FCSTD DOCUMENT  (FreeCAD 0.19R23578 (Git))
Label: enclosure_assembly
License: All rights reserved
LicenseURL: http://en.wikipedia.org/wiki/All_rights_reserved
objects: App::Link×8, App::DocumentObjectGroup×2, PartDesign::CoordinateSystem×1, App::FeaturePython×1, App::Part×1
note: 1 computed .brp shape members not serialized (recipe doc carries the construction recipe); baked Part::Feature solids carry a one-line shape summary decoded from their .brp
EXTERNAL_REF file=enclosure_sheetmetal.FCStd obj=LCS_4
EXTERNAL_REF file=enclosure_sheetmetal.FCStd obj=Body
EXTERNAL_REF file=enclosure_sheetmetal.FCStd obj=LCS_5
EXTERNAL_REF file=enclosure_windows.FCStd obj=LCS_1
EXTERNAL_REF file=enclosure_windows.FCStd obj=Body001
EXTERNAL_REF file=enclosure_hinges.FCStd obj=LCS_1
EXTERNAL_REF file=enclosure_sheetmetal.FCStd obj=LCS_7
EXTERNAL_REF file=enclosure_hinges.FCStd obj=Body001
EXTERNAL_REF file=enclosure_sheetmetal.FCStd obj=LCS_6
EXTERNAL_REF file=enclosure_hinges.FCStd obj=LCS_4
EXTERNAL_REF file=enclosure_hinges.FCStd obj=LCS_7
EXTERNAL_REF file=enclosure_hinges.FCStd obj=Body002
EXTERNAL_REF file=enclosure_hinges.FCStd obj=LCS_6
EXTERNAL_REF file=enclosure_sheetmetal.FCStd obj=LCS_3
EXTERNAL_REF file=enclosure_sheetmetal.FCStd obj=LCS_2
EXTERNAL_REF file=enclosure_sheetmetal.FCStd obj=Body001
EXTERNAL_REF file=enclosure_sheetmetal.FCStd obj=LCS_1
EXTERNAL_REF file=enclosure_windows.FCStd obj=LCS_2
EXTERNAL_REF file=enclosure_windows.FCStd obj=Body

FEATURE [App::DocumentObjectGroup] Parts
FEATURE [PartDesign::CoordinateSystem] LCS_Origin
  AttacherType = Attacher::AttachEngine3D
  MapMode = 2
  Support = -> [X_Axis]
FEATURE [App::DocumentObjectGroup] Constraints
FEATURE [App::FeaturePython] Variables  # WARN: FeaturePython — macro-defined, semantics opaque (R4)
FEATURE [App::Link] enclosure_sheetmetal_main_housing
  AssemblyType = Asm4EE
  AttachedBy = #LCS_4
  AttachedTo = Parent Assembly#LCS_Origin
  AttachmentOffset = pos=(0,0,0) rot=(0.707107,0,0.707107;3.14159rad)
  LinkPlacement = pos=(0,304.8,-3.73e-14) rot=(0.707107,0,0.707107;3.14159rad)
  LinkedObject = -> <external enclosure_sheetmetal.FCStd>#Body
  Placement = pos=(0,304.8,-3.73e-14) rot=(0.707107,0,0.707107;3.14159rad)
  expr: Placement = LCS_Origin.Placement * AttachmentOffset * enclosure_sheetmetal#LCS_4.Placement ^ -1
FEATURE [App::Link] enclosure_windows_top_acrylic_panel
  AssemblyType = Asm4EE
  AttachedBy = #LCS_1
  AttachedTo = enclosure_sheetmetal_main_housing#LCS_5
  AttachmentOffset = pos=(0,0,0) rot=(0,0,1;1.5708rad)
  LinkPlacement = pos=(298,2.6933e-12,573.5) rot=(0,0,-1;4.71239rad)
  LinkedObject = -> <external enclosure_windows.FCStd>#Body001
  Placement = pos=(298,2.6933e-12,573.5) rot=(0,0,-1;4.71239rad)
  expr: Placement = enclosure_sheetmetal_main_housing.Placement * enclosure_sheetmetal#LCS_5.Placement * AttachmentOffset * enclosure_windows#LCS_1.Placement ^ -1
FEATURE [App::Link] enclosure_hinges_Hinge_A
  AssemblyType = Asm4EE
  AttachedBy = #LCS_1
  AttachedTo = enclosure_sheetmetal_main_housing#LCS_7
  LinkPlacement = pos=(107.95,-306.8,514.35) rot=(-1,0,0;4.71239rad)
  LinkedObject = -> <external enclosure_hinges.FCStd>#Body001
  Placement = pos=(107.95,-306.8,514.35) rot=(-1,0,0;4.71239rad)
  expr: Placement = enclosure_sheetmetal_main_housing.Placement * enclosure_sheetmetal#LCS_7.Placement * AttachmentOffset * enclosure_hinges#LCS_1.Placement ^ -1
FEATURE [App::Link] enclosure_hinges_Hinge_A001
  AssemblyType = Asm4EE
  AttachedBy = #LCS_1
  AttachedTo = enclosure_sheetmetal_main_housing#LCS_6
  LinkPlacement = pos=(107.95,-306.8,95.25) rot=(-1,0,0;4.71239rad)
  LinkedObject = -> <external enclosure_hinges.FCStd>#Body001
  Placement = pos=(107.95,-306.8,95.25) rot=(-1,0,0;4.71239rad)
  expr: Placement = enclosure_sheetmetal_main_housing.Placement * enclosure_sheetmetal#LCS_6.Placement * AttachmentOffset * enclosure_hinges#LCS_1.Placement ^ -1
FEATURE [App::Link] enclosure_hinges_Hinge_B
  AssemblyType = Asm4EE
  AttachedBy = #LCS_7
  AttachedTo = enclosure_hinges_Hinge_A#LCS_4
  LinkPlacement = pos=(127,-325.85,476.25) rot=(0.57735,0.57735,-0.57735;4.18879rad)
  LinkedObject = -> <external enclosure_hinges.FCStd>#Body002
  Placement = pos=(127,-325.85,476.25) rot=(0.57735,0.57735,-0.57735;4.18879rad)
  expr: Placement = enclosure_hinges_Hinge_A.Placement * enclosure_hinges#LCS_4.Placement * AttachmentOffset * enclosure_hinges#LCS_7.Placement ^ -1
FEATURE [App::Link] enclosure_hinges_Hinge_B001
  AssemblyType = Asm4EE
  AttachedBy = #LCS_6
  AttachedTo = enclosure_sheetmetal_door#LCS_3
  AttachmentOffset = pos=(0,0,0) rot=(1,0,0;3.14159rad)
  LinkPlacement = pos=(127,-325.85,57.15) rot=(-0.57735,-0.57735,0.57735;2.0944rad)
  LinkedObject = -> <external enclosure_hinges.FCStd>#Body002
  Placement = pos=(127,-325.85,57.15) rot=(-0.57735,-0.57735,0.57735;2.0944rad)
  expr: Placement = enclosure_sheetmetal_door.Placement * enclosure_sheetmetal#LCS_3.Placement * AttachmentOffset * enclosure_hinges#LCS_6.Placement ^ -1
FEATURE [App::Link] enclosure_sheetmetal_door
  AssemblyType = Asm4EE
  AttachedBy = #LCS_2
  AttachedTo = enclosure_hinges_Hinge_B#LCS_6
  AttachmentOffset = pos=(0,0,0) rot=(1,0,0;3.14159rad)
  LinkPlacement = pos=(129,-346.9,571.5) rot=(1,0,0;4.71239rad)
  LinkedObject = -> <external enclosure_sheetmetal.FCStd>#Body001
  Placement = pos=(129,-346.9,571.5) rot=(1,0,0;4.71239rad)
  expr: Placement = enclosure_hinges_Hinge_B.Placement * enclosure_hinges#LCS_6.Placement * AttachmentOffset * enclosure_sheetmetal#LCS_2.Placement ^ -1
FEATURE [App::Link] enclosure_windows_side_acrylic_panel
  AssemblyType = Asm4EE
  AttachedBy = #LCS_2
  AttachedTo = enclosure_sheetmetal_door#LCS_1
  AttachmentOffset = pos=(0,0,0) rot=(0,0,1;3.14159rad)
  LinkPlacement = pos=(757.6,-346.9,284.75) rot=(0,-0.707107,-0.707107;3.14159rad)
  LinkedObject = -> <external enclosure_windows.FCStd>#Body
  Placement = pos=(757.6,-346.9,284.75) rot=(0,-0.707107,-0.707107;3.14159rad)
  expr: Placement = enclosure_sheetmetal_door.Placement * enclosure_sheetmetal#LCS_1.Placement * AttachmentOffset * enclosure_windows#LCS_2.Placement ^ -1
FEATURE [App::Part] Model
  Configuration = 0
  Group = -> [LCS_Origin,Constraints,Variables,enclosure_sheetmetal_main_housing,enclosure_windows_top_acrylic_panel,enclosure_hinges_Hinge_A,enclosure_hinges_Hinge_A001,enclosure_hinges_Hinge_B,enclosure_hinges_Hinge_B001,enclosure_sheetmetal_door,enclosure_windows_side_acrylic_panel]
  Origin = -> Origin
  Type = Assembly4 Model

RESOLVED EXTERNAL PARTS (link-assembly join: the EXTERNAL_REF files above that resolve inside this repo's crawl, each included once):
---- part enclosure_hinges.FCStd = doc fcstd_d395666c116b ----
FCSTD DOCUMENT  (FreeCAD 0.19R23578 (Git))
Label: enclosure_hinges
License: All rights reserved
LicenseURL: http://en.wikipedia.org/wiki/All_rights_reserved
objects: PartDesign::CoordinateSystem×11, Sketcher::SketchObject×10, PartDesign::Fillet×5, PartDesign::Pocket×4, PartDesign::Pad×3, PartDesign::Body×3, PartDesign::Hole×2, PartDesign::Revolution×1
note: 54 computed .brp shape members not serialized (recipe doc carries the construction recipe); baked Part::Feature solids carry a one-line shape summary decoded from their .brp

FEATURE [Sketcher::SketchObject] Sketch004
  MapMode = 5
  Placement = pos=(0,0,0) rot=(1,0,0;1.5708rad)
  Support = -> [XZ_Plane003]
  expr: Constraints[7] = 0.375"
  expr: Constraints[8] = 0.375"
  sketch-geometry (7):
    g0: LineSegment StartX=-8.37762 StartY=2.44 StartZ=0 EndX=6.54086 EndY=13.5368 EndZ=0
    g1: ArcOfCircle CenterX=9.525 CenterY=9.525 CenterZ=0 NormalX=0 NormalY=0 NormalZ=1 AngleXU=0 Radius=5 StartAngle=5.35193 EndAngle=8.49352
    g2: LineSegment StartX=12.5091 StartY=5.51315 StartZ=0 EndX=8.37762 EndY=2.44 EndZ=0
    g3: LineSegment StartX=8.37762 StartY=2.44 StartZ=0 EndX=8.37762 EndY=0 EndZ=0
    g4: Circle CenterX=9.525 CenterY=9.525 CenterZ=0 NormalX=0 NormalY=0 NormalZ=1 AngleXU=0 Radius=2.55
    g5: LineSegment StartX=-8.37762 StartY=2.44 StartZ=0 EndX=-8.37762 EndY=0 EndZ=0
    g6: LineSegment StartX=8.37762 StartY=0 StartZ=0 EndX=-8.37762 EndY=0 EndZ=0
  constraints (18):
    c: Coincident(g3,g2)
    c: Vertical(g3)
    c: Tangent(g2,g1) = 1.5708
    c: Tangent(g1,g0) = 1.5708
    c: Diameter(g1) = 10
    c: Coincident(g4,g1)
    c: Diameter(g4) = 5.1
    c: DistanceX(g-1,g1) = 9.525
    c: DistanceY(g-1,g1) = 9.525
    c: Parallel(g0,g2)
    c: Coincident(g5,g0)
    c: PointOnObject(g5,g-1)
    c: Coincident(g6,g3)
    c: Coincident(g6,g5)
    c: Vertical(g5)
    c: Equal(g5,g3)
    c: DistanceY(g3,g3) = 2.44
    c: Symmetric(g5,g3,g-2)
FEATURE [PartDesign::Pad] Pad001
  Direction = (1,1,1)
  Length = 38.1
  Length2 = 100
  Placement = pos=(0,0,0) rot=(1,0,0;1.5708rad)
  Profile = -> Sketch004
  Type = 0
  expr: Length = 1.5"
FEATURE [Sketcher::SketchObject] Sketch005
  AttachmentOffset = pos=(0,0,22.44) rot=(0,0,1;0rad)
  MapMode = 5
  Placement = pos=(0,0,22.44) rot=(0,0,1;0rad)
  Support = -> [XY_Plane003]
  expr: Constraints[8] = Pad001.Length / 2
  expr: Constraints[10] = 5.25mm
  sketch-geometry (4):
    g0: Circle CenterX=0 CenterY=-6.35 CenterZ=0 NormalX=0 NormalY=0 NormalZ=1 AngleXU=0 Radius=2.625
    g1: Circle CenterX=0 CenterY=-31.75 CenterZ=0 NormalX=0 NormalY=0 NormalZ=1 AngleXU=0 Radius=2.625
    g2: LineSegment StartX=0 StartY=-6.35 StartZ=0 EndX=0 EndY=-19.05 EndZ=0
    g3: LineSegment StartX=0 StartY=-19.05 StartZ=0 EndX=0 EndY=-31.75 EndZ=0
  constraints (11):
    c: PointOnObject(g0,g-2)
    c: PointOnObject(g1,g-2)
    c: DistanceY(g1,g0) = 25.4
    c: Coincident(g2,g0)
    c: PointOnObject(g2,g-2)
    c: Coincident(g3,g2)
    c: Coincident(g3,g1)
    c: Equal(g2,g3)
    c: DistanceY(g2,g-1) = 19.05
    c: Equal(g0,g1)
    c: Diameter(g0) = 5.25
FEATURE [PartDesign::Hole] Hole001
  BaseFeature = -> Pad001
  Depth = 25
  DepthType = 1
  Diameter = 6
  DrillPoint = 1
  DrillPointAngle = 118
  HoleCutCountersinkAngle = 90
  HoleCutDepth = 20
  HoleCutDiameter = 11
  HoleCutType = 1
  ModelActualThread = false
  Placement = pos=(0,0,0) rot=(1,0,0;1.5708rad)
  Profile = -> Sketch005
  Tapered = false
  TaperedAngle = 90
  ThreadAngle = 0
  ThreadClass = 0
  ThreadCutOffInner = 0
  ThreadCutOffOuter = 0
  ThreadDirection = 0
  ThreadFit = 0
  ThreadPitch = 0
  ThreadSize = 0
  ThreadType = 0
  Threaded = false
FEATURE [Sketcher::SketchObject] Sketch006
  MapMode = 5
  Placement = pos=(0,0,0) rot=(0.57735,0.57735,0.57735;2.0944rad)
  Support = -> [YZ_Plane003]
  expr: Constraints[11] = Pad001.Length / 2
  expr: Constraints[8] = Pad001.Length / 3
  sketch-geometry (5):
    g0: LineSegment StartX=-12.7 StartY=2.44 StartZ=0 EndX=-25.4 EndY=2.44 EndZ=0
    g1: LineSegment StartX=-25.4 StartY=2.44 StartZ=0 EndX=-25.4 EndY=22.44 EndZ=0
    g2: LineSegment StartX=-25.4 StartY=22.44 StartZ=0 EndX=-12.7 EndY=22.44 EndZ=0
    g3: LineSegment StartX=-12.7 StartY=22.44 StartZ=0 EndX=-12.7 EndY=2.44 EndZ=0
    g4: LineSegment StartX=-19.05 StartY=22.44 StartZ=0 EndX=-19.05 EndY=2.44 EndZ=0
  constraints (15):
    c: Coincident(g0,g1)
    c: Coincident(g1,g2)
    c: Coincident(g2,g3)
    c: Coincident(g3,g0)
    c: Horizontal(g0)
    c: Horizontal(g2)
    c: Vertical(g1)
    c: Vertical(g3)
    c: DistanceX(g2,g2) = 12.7
    c: PointOnObject(g4,g2)
    c: PointOnObject(g4,g0)
    c: DistanceX(g4,g-1) = 19.05
    c: Symmetric(g2,g1,g4)
    c: DistanceY(g3,g3) = 20
    c: DistanceY(g-1,g0) = 2.44
FEATURE [PartDesign::Pocket] Pocket001
  BaseFeature = -> Hole001
  Length = 5
  Length2 = 100
  Midplane = true
  Placement = pos=(0,0,0) rot=(1,0,0;1.5708rad)
  Profile = -> Sketch006
  Type = 1
FEATURE [Sketcher::SketchObject] Sketch007
  AttachmentOffset = pos=(0,0,22.44) rot=(0,0,1;0rad)
  MapMode = 5
  Placement = pos=(0,0,22.44) rot=(0,0,1;0rad)
  Support = -> [XY_Plane004]
  expr: Constraints[10] = 5.25mm
  expr: Constraints[8] = Pad002.Length / 2
  sketch-geometry (4):
    g0: Circle CenterX=0 CenterY=-6.35 CenterZ=0 NormalX=0 NormalY=0 NormalZ=1 AngleXU=0 Radius=2.625
    g1: Circle CenterX=0 CenterY=-31.75 CenterZ=0 NormalX=0 NormalY=0 NormalZ=1 AngleXU=0 Radius=2.625
    g2: LineSegment StartX=0 StartY=-6.35 StartZ=0 EndX=0 EndY=-19.05 EndZ=0
    g3: LineSegment StartX=0 StartY=-19.05 StartZ=0 EndX=0 EndY=-31.75 EndZ=0
  constraints (11):
    c: PointOnObject(g0,g-2)
    c: PointOnObject(g1,g-2)
    c: DistanceY(g1,g0) = 25.4
    c: Coincident(g2,g0)
    c: PointOnObject(g2,g-2)
    c: Coincident(g3,g2)
    c: Coincident(g3,g1)
    c: Equal(g2,g3)
    c: DistanceY(g2,g-1) = 19.05
    c: Equal(g0,g1)
    c: Diameter(g0) = 5.25
FEATURE [Sketcher::SketchObject] Sketch008
  MapMode = 5
  Placement = pos=(0,0,0) rot=(0.57735,0.57735,0.57735;2.0944rad)
  Support = -> [YZ_Plane004]
  expr: Constraints[26] = Pad002.Length / 3 - 0.24mm
  expr: Constraints[24] = Pad002.Length / 2
  sketch-geometry (9):
    g0: LineSegment StartX=-25.28 StartY=2.44 StartZ=0 EndX=-45.28 EndY=2.44 EndZ=0
    g1: LineSegment StartX=-45.28 StartY=2.44 StartZ=0 EndX=-45.28 EndY=22.44 EndZ=0
    g2: LineSegment StartX=-45.28 StartY=22.44 StartZ=0 EndX=-25.28 EndY=22.44 EndZ=0
    g3: LineSegment StartX=-25.28 StartY=22.44 StartZ=0 EndX=-25.28 EndY=2.44 EndZ=0
    g4: LineSegment StartX=-12.82 StartY=2.44 StartZ=0 EndX=7.18 EndY=2.44 EndZ=0
    g5: LineSegment StartX=7.18 StartY=2.44 StartZ=0 EndX=7.18 EndY=22.44 EndZ=0
    g6: LineSegment StartX=7.18 StartY=22.44 StartZ=0 EndX=-12.82 EndY=22.44 EndZ=0
    g7: LineSegment StartX=-12.82 StartY=22.44 StartZ=0 EndX=-12.82 EndY=2.44 EndZ=0
    g8: LineSegment StartX=-19.05 StartY=22.44 StartZ=0 EndX=-19.05 EndY=2.44 EndZ=0
  constraints (27):
    c: Coincident(g0,g1)
    c: Coincident(g1,g2)
    c: Coincident(g2,g3)
    c: Coincident(g3,g0)
    c: Horizontal(g0)
    c: Horizontal(g2)
    c: Vertical(g1)
    c: Vertical(g3)
    c: Coincident(g4,g5)
    c: Coincident(g5,g6)
    c: Coincident(g6,g7)
    c: Coincident(g7,g4)
    c: Horizontal(g4)
    c: Horizontal(g6)
    c: Vertical(g5)
    c: Vertical(g7)
    c: Horizontal(g6,g2)
    c: Horizontal(g0,g4)
    c: Equal(g4,g0)
    c: DistanceY(g1,g1) = 20
    c: DistanceX(g2,g2) = 20
    c: Horizontal(g8,g2)
    c: Horizontal(g0,g8)
    c: Symmetric(g6,g2,g8)
    c: DistanceX(g8,g-1) = 19.05
    c: DistanceY(g-1,g4) = 2.44
    c: DistanceX(g2,g6) = 12.46
FEATURE [Sketcher::SketchObject] Sketch009
  MapMode = 5
  Placement = pos=(0,0,0) rot=(1,0,0;1.5708rad)
  Support = -> [XZ_Plane005]
  expr: Constraints[8] = 0.375"
  expr: Constraints[7] = 0.375"
  sketch-geometry (7):
    g0: LineSegment StartX=-8.37762 StartY=2.44 StartZ=0 EndX=6.54086 EndY=13.5368 EndZ=0
    g1: ArcOfCircle CenterX=9.525 CenterY=9.525 CenterZ=0 NormalX=0 NormalY=0 NormalZ=1 AngleXU=0 Radius=5 StartAngle=5.35193 EndAngle=8.49352
    g2: LineSegment StartX=12.5091 StartY=5.51315 StartZ=0 EndX=8.37762 EndY=2.44 EndZ=0
    g3: LineSegment StartX=8.37762 StartY=2.44 StartZ=0 EndX=8.37762 EndY=0 EndZ=0
    g4: Circle CenterX=9.525 CenterY=9.525 CenterZ=0 NormalX=0 NormalY=0 NormalZ=1 AngleXU=0 Radius=2.55
    g5: LineSegment StartX=-8.37762 StartY=2.44 StartZ=0 EndX=-8.37762 EndY=0 EndZ=0
    g6: LineSegment StartX=8.37762 StartY=0 StartZ=0 EndX=-8.37762 EndY=0 EndZ=0
  constraints (18):
    c: Coincident(g3,g2)
    c: Vertical(g3)
    c: Tangent(g2,g1) = 1.5708
    c: Tangent(g1,g0) = 1.5708
    c: Diameter(g1) = 10
    c: Coincident(g4,g1)
    c: Diameter(g4) = 5.1
    c: DistanceX(g-1,g1) = 9.525
    c: DistanceY(g-1,g1) = 9.525
    c: Parallel(g0,g2)
    c: Coincident(g5,g0)
    c: PointOnObject(g5,g-1)
    c: Coincident(g6,g3)
    c: Coincident(g6,g5)
    c: Vertical(g5)
    c: Equal(g5,g3)
    c: DistanceY(g3,g3) = 2.44
    c: Symmetric(g5,g3,g-2)
FEATURE [PartDesign::Pad] Pad002
  Direction = (1,1,1)
  Length = 38.1
  Length2 = 100
  Placement = pos=(0,0,0) rot=(1,0,0;1.5708rad)
  Profile = -> Sketch009
  Type = 0
  expr: Length = 1.5"
FEATURE [PartDesign::Hole] Hole002
  BaseFeature = -> Pad002
  Depth = 25
  DepthType = 1
  Diameter = 6
  DrillPoint = 1
  DrillPointAngle = 118
  HoleCutCountersinkAngle = 90
  HoleCutDepth = 20
  HoleCutDiameter = 11
  HoleCutType = 1
  ModelActualThread = false
  Placement = pos=(0,0,0) rot=(1,0,0;1.5708rad)
  Profile = -> Sketch007
  Tapered = false
  TaperedAngle = 90
  ThreadAngle = 0
  ThreadClass = 0
  ThreadCutOffInner = 0
  ThreadCutOffOuter = 0
  ThreadDirection = 0
  ThreadFit = 0
  ThreadPitch = 0
  ThreadSize = 0
  ThreadType = 0
  Threaded = false
FEATURE [PartDesign::Pocket] Pocket002
  BaseFeature = -> Hole002
  Length = 5
  Length2 = 100
  Midplane = true
  Placement = pos=(0,0,0) rot=(1,0,0;1.5708rad)
  Profile = -> Sketch008
  Type = 1
FEATURE [PartDesign::Fillet] Fillet
  Base = -> Pocket002 [Edge33,Edge18,Edge17,Edge32]
  BaseFeature = -> Pocket002
  Placement = pos=(0,0,0) rot=(1,0,0;1.5708rad)
  Radius = 1
  SupportTransform = true
FEATURE [PartDesign::Fillet] Fillet001
  Base = -> Pocket001 [Edge20,Edge10]
  BaseFeature = -> Pocket001
  Placement = pos=(0,0,0) rot=(1,0,0;1.5708rad)
  Radius = 1
  SupportTransform = true
FEATURE [PartDesign::Fillet] Fillet002
  Base = -> Fillet001 [Edge36,Edge21]
  BaseFeature = -> Fillet001
  Placement = pos=(0,0,0) rot=(1,0,0;1.5708rad)
  Radius = 1
  SupportTransform = true
FEATURE [PartDesign::Fillet] Fillet003
  Base = -> Fillet [Edge9,Edge28]
  BaseFeature = -> Fillet
  Placement = pos=(0,0,0) rot=(1,0,0;1.5708rad)
  Radius = 1
  SupportTransform = true
FEATURE [Sketcher::SketchObject] Sketch
  MapMode = 5
  Support = -> [XY_Plane006]
  expr: Constraints[11] = 1.5in
  sketch-geometry (7):
    g0: LineSegment StartX=2.55 StartY=19.05 StartZ=0 EndX=5 EndY=19.05 EndZ=0
    g1: LineSegment StartX=5 StartY=19.05 StartZ=0 EndX=19.6187 EndY=4.43129 EndZ=0
    g2: LineSegment StartX=19.6187 StartY=4.43129 StartZ=0 EndX=19.6187 EndY=-4.43129 EndZ=0
    g3: LineSegment StartX=19.6187 StartY=-4.43129 StartZ=0 EndX=5 EndY=-19.05 EndZ=0
    g4: LineSegment StartX=5 StartY=-19.05 StartZ=0 EndX=2.55 EndY=-19.05 EndZ=0
    g5: LineSegment StartX=2.55 StartY=-19.05 StartZ=0 EndX=2.55 EndY=19.05 EndZ=0
    g6: LineSegment StartX=-9.05314 StartY=0 StartZ=0 EndX=28.1994 EndY=0 EndZ=0
  constraints (16):
    c: Horizontal(g0)
    c: Coincident(g0,g1)
    c: Coincident(g1,g2)
    c: Coincident(g2,g3)
    c: Coincident(g3,g4)
    c: Coincident(g4,g5)
    c: Coincident(g5,g0)
    c: Horizontal(g6)
    c: Symmetric(g0,g4,g6)
    c: Symmetric(g3,g0,g6)
    c: Symmetric(g1,g2,g6)
    c: DistanceY(g5,g5) = 38.1
    c: DistanceX(g-1,g0) = 2.55
    c: Angle(g5,g1) = 0.785398
    c: DistanceX(g-1,g0) = 5
    c: PointOnObject(g6,g-1)
FEATURE [PartDesign::Revolution] Revolution
  Angle = 360
  Axis = (0,1,0)
  Base = (0,0,0)
  Profile = -> Sketch
  ReferenceAxis = -> Sketch [V_Axis]
  Reversed = true
FEATURE [Sketcher::SketchObject] Sketch010
  MapMode = 5
  Placement = pos=(0,0,0) rot=(1,0,0;1.5708rad)
  Support = -> [XZ_Plane006]
  sketch-geometry (8):
    g0: ArcOfCircle CenterX=0 CenterY=0 CenterZ=0 NormalX=0 NormalY=0 NormalZ=1 AngleXU=0 Radius=5 StartAngle=1.5708 EndAngle=4.71239
    g1: LineSegment StartX=3e-16 StartY=5 StartZ=0 EndX=76.4224 EndY=5 EndZ=0
    g2: LineSegment StartX=76.4224 StartY=5 StartZ=0 EndX=76.4224 EndY=50.1076 EndZ=0
    g3: LineSegment StartX=76.4224 StartY=50.1076 StartZ=0 EndX=-42.6385 EndY=50.1076 EndZ=0
    g4: LineSegment StartX=-42.6385 StartY=50.1076 StartZ=0 EndX=-42.6385 EndY=-50.303 EndZ=0
    g5: LineSegment StartX=-42.6385 StartY=-50.303 StartZ=0 EndX=76.4224 EndY=-50.303 EndZ=0
    g6: LineSegment StartX=76.4224 StartY=-50.303 StartZ=0 EndX=76.4224 EndY=-5 EndZ=0
    g7: LineSegment StartX=76.4224 StartY=-5 StartZ=0 EndX=0 EndY=-5 EndZ=0
  constraints (20):
    c: Coincident(g0,g-1)
    c: PointOnObject(g0,g-2)
    c: PointOnObject(g0,g-2)
    c: Coincident(g1,g0)
    c: Horizontal(g1)
    c: Coincident(g1,g2)
    c: Vertical(g2)
    c: Coincident(g2,g3)
    c: Horizontal(g3)
    c: Coincident(g3,g4)
    c: Vertical(g4)
    c: Coincident(g4,g5)
    c: Horizontal(g5)
    c: Coincident(g5,g6)
    c: Coincident(g6,g7)
    c: Coincident(g7,g0)
    c: Horizontal(g7)
    c: Vertical(g6)
    c: Vertical(g6,g1)
    c: Radius(g0) = 5
FEATURE [PartDesign::Pocket] Pocket
  BaseFeature = -> Revolution
  Length = 5
  Length2 = 100
  Midplane = true
  Profile = -> Sketch010
  Type = 1
FEATURE [Sketcher::SketchObject] Sketch011
  MapMode = 5
  Placement = pos=(0,0,0) rot=(1,0,0;1.5708rad)
  Support = -> [XZ_Plane006]
  expr: Constraints[11] = 1in
  sketch-geometry (5):
    g0: Circle CenterX=25.4 CenterY=0 CenterZ=0 NormalX=0 NormalY=0 NormalZ=1 AngleXU=0 Radius=2.55
    g1: ArcOfCircle CenterX=25.4 CenterY=0 CenterZ=0 NormalX=0 NormalY=0 NormalZ=1 AngleXU=0 Radius=5 StartAngle=4.71239 EndAngle=7.85398
    g2: LineSegment StartX=25.4 StartY=5 StartZ=0 EndX=7 EndY=5 EndZ=0
    g3: LineSegment StartX=7 StartY=5 StartZ=0 EndX=7 EndY=-5 EndZ=0
    g4: LineSegment StartX=7 StartY=-5 StartZ=0 EndX=25.4 EndY=-5 EndZ=0
  constraints (13):
    c: PointOnObject(g0,g-1)
    c: Coincident(g1,g0)
    c: Tangent(g1,g2) = -1.5708
    c: Coincident(g2,g3)
    c: Coincident(g3,g4)
    c: Tangent(g4,g1) = -1.5708
    c: Horizontal(g2)
    c: Horizontal(g4)
    c: Vertical(g3)
    c: Diameter(g0) = 5.1
    c: Diameter(g1) = 10
    c: DistanceX(g-1,g0) = 25.4
    c: DistanceX(g-1,g2) = 7
FEATURE [PartDesign::Pad] Pad
  BaseFeature = -> Pocket
  Direction = (1,1,1)
  Length = 12.46
  Length2 = 100
  Midplane = true
  Profile = -> Sketch011
  Type = 0
  expr: Length = Pad002.Length / 3 - 0.24mm
FEATURE [Sketcher::SketchObject] Sketch012
  MapMode = 5
  Support = -> [XY_Plane006]
  expr: Constraints[12] = Pad001.Length / 3
  sketch-geometry (6):
    g0: LineSegment StartX=-20.0307 StartY=6.35 StartZ=0 EndX=5 EndY=6.35 EndZ=0
    g1: LineSegment StartX=6 StartY=5.35 StartZ=0 EndX=6 EndY=-5.35 EndZ=0
    g2: LineSegment StartX=5 StartY=-6.35 StartZ=0 EndX=-20.0307 EndY=-6.35 EndZ=0
    g3: LineSegment StartX=-20.0307 StartY=-6.35 StartZ=0 EndX=-20.0307 EndY=6.35 EndZ=0
    g4: ArcOfCircle CenterX=5 CenterY=5.35 CenterZ=0 NormalX=0 NormalY=0 NormalZ=1 AngleXU=0 Radius=1 StartAngle=0 EndAngle=1.5708
    g5: ArcOfCircle CenterX=5 CenterY=-5.35 CenterZ=0 NormalX=0 NormalY=0 NormalZ=1 AngleXU=0 Radius=1 StartAngle=4.71239 EndAngle=6.28319
  constraints (14):
    c: Coincident(g2,g3)
    c: Coincident(g3,g0)
    c: Horizontal(g0)
    c: Horizontal(g2)
    c: Vertical(g1)
    c: Symmetric(g0,g2,g-1)
    c: Tangent(g0,g4) = 1.5708
    c: Tangent(g1,g4) = 1.5708
    c: Tangent(g1,g5) = 1.5708
    c: Tangent(g2,g5) = 1.5708
    c: Radius(g5) = 1
    c: Equal(g4,g5)
    c: DistanceY(g3,g3) = 12.7
    c: DistanceX(g-1,g1) = 6
FEATURE [PartDesign::Pocket] Pocket003
  BaseFeature = -> Pad
  Length = 5
  Length2 = 100
  Midplane = true
  Profile = -> Sketch012
  Type = 1
FEATURE [PartDesign::Fillet] Fillet004
  Base = -> Pocket003 [Edge14,Edge8,Edge55,Edge63]
  BaseFeature = -> Pocket003
  Radius = 2
  SupportTransform = false
FEATURE [PartDesign::CoordinateSystem] LCS_1
  AttacherType = Attacher::AttachEngine3D
  MapMode = 45
  Placement = pos=(2e-16,-19.05,0) rot=(0,0,1;0rad)
  Support = -> [Pad001]
FEATURE [PartDesign::CoordinateSystem] LCS_2
  AttacherType = Attacher::AttachEngine3D
  MapMode = 11
  Placement = pos=(0,-6.35,2.44) rot=(0,0,1;1.5708rad)
  Support = -> [Hole001]
FEATURE [PartDesign::CoordinateSystem] LCS_3
  AttacherType = Attacher::AttachEngine3D
  MapMode = 11
  Placement = pos=(0,-31.75,2.44) rot=(0,0,1;1.5708rad)
  Support = -> [Hole001]
FEATURE [PartDesign::CoordinateSystem] LCS_4
  AttacherType = Attacher::AttachEngine3D
  MapMode = 45
  Placement = pos=(9.525,-19.05,9.525) rot=(0,0.707107,0.707107;3.14159rad)
  Support = -> [Pad001]
FEATURE [PartDesign::CoordinateSystem] LCS_5
  AttacherType = Attacher::AttachEngine3D
  AttachmentOffset = pos=(0,0,19.05) rot=(0,0,1;0rad)
  MapMode = 11
  Placement = pos=(9.525,-19.05,9.525) rot=(0.57735,-0.57735,0.57735;2.0944rad)
  Support = -> [Sketch004]
  expr: .AttachmentOffset.Base.z = 0.5 * Pad001.Length
FEATURE [PartDesign::Body] Body001  label="Hinge_A"
  Group = -> [Sketch004,Pad001,Sketch005,Hole001,Sketch006,Pocket001,Fillet001,Fillet002,LCS_1,LCS_2,LCS_3,LCS_4,LCS_5]
  Origin = -> Origin003
  Tip = -> Fillet002
FEATURE [PartDesign::CoordinateSystem] LCS_6
  AttacherType = Attacher::AttachEngine3D
  MapMode = 45
  Placement = pos=(2e-16,-19.05,0) rot=(0,0,1;0rad)
  Support = -> [Pad002]
FEATURE [PartDesign::CoordinateSystem] LCS_7
  AttacherType = Attacher::AttachEngine3D
  AttachmentOffset = pos=(0,0,19.05) rot=(0,0,1;0rad)
  MapMode = 11
  Placement = pos=(9.525,-19.05,9.525) rot=(0.57735,-0.57735,0.57735;2.0944rad)
  Support = -> [Sketch009]
  expr: .AttachmentOffset.Base.z = Pad002.Length / 2
FEATURE [PartDesign::CoordinateSystem] LCS_8
  AttacherType = Attacher::AttachEngine3D
  MapMode = 11
  Placement = pos=(0,-6.35,2.44) rot=(0,0,1;1.5708rad)
  Support = -> [Hole002]
FEATURE [PartDesign::CoordinateSystem] LCS_9
  AttacherType = Attacher::AttachEngine3D
  MapMode = 11
  Placement = pos=(0,-31.75,2.44) rot=(0,0,1;1.5708rad)
  Support = -> [Hole002]
FEATURE [PartDesign::Body] Body002  label="Hinge_B"
  Group = -> [Sketch009,Pad002,Sketch007,Hole002,Sketch008,Pocket002,Fillet,Fillet003,LCS_6,LCS_7,LCS_8,LCS_9]
  Origin = -> Origin005
  Tip = -> Fillet003
FEATURE [PartDesign::CoordinateSystem] LCS_10
  AttacherType = Attacher::AttachEngine3D
  MapMode = 5
  Support = -> [XY_Plane006]
FEATURE [PartDesign::CoordinateSystem] LCS_11
  AttacherType = Attacher::AttachEngine3D
  MapMode = 11
  Placement = pos=(25.4,0,0) rot=(0.57735,-0.57735,0.57735;2.0944rad)
  Support = -> [Sketch011]
FEATURE [PartDesign::Body] Body  label="Hinge_C"
  Group = -> [Sketch,Revolution,Sketch010,Pocket,Sketch011,Pad,Sketch012,Pocket003,Fillet004,LCS_10,LCS_11]
  Origin = -> Origin006
  Tip = -> Fillet004
---- part enclosure_sheetmetal.FCStd = doc fcstd_4c1e4707e105 ----
FCSTD DOCUMENT  (FreeCAD 0.19R23578 (Git))
Label: enclosure_sheetmetal
License: All rights reserved
LicenseURL: http://en.wikipedia.org/wiki/All_rights_reserved
objects: PartDesign::FeaturePython×10, Sketcher::SketchObject×7, PartDesign::CoordinateSystem×7, PartDesign::Pocket×5, PartDesign::Body×2, PartDesign::Chamfer×1
note: 38 computed .brp shape members not serialized (recipe doc carries the construction recipe); baked Part::Feature solids carry a one-line shape summary decoded from their .brp

FEATURE [Sketcher::SketchObject] Sketch
  MapMode = 5
  Support = -> [XY_Plane001]
  expr: Constraints[9] = 24"
  expr: Constraints[10] = 22.5"
  sketch-geometry (4):
    g0: LineSegment StartX=0 StartY=0 StartZ=0 EndX=571.5 EndY=0 EndZ=0
    g1: LineSegment StartX=571.5 StartY=0 StartZ=0 EndX=571.5 EndY=609.6 EndZ=0
    g2: LineSegment StartX=571.5 StartY=609.6 StartZ=0 EndX=0 EndY=609.6 EndZ=0
    g3: LineSegment StartX=0 StartY=609.6 StartZ=0 EndX=0 EndY=0 EndZ=0
  constraints (11):
    c: Coincident(g0,g1)
    c: Coincident(g1,g2)
    c: Coincident(g2,g3)
    c: Coincident(g3,g0)
    c: Horizontal(g0)
    c: Horizontal(g2)
    c: Vertical(g1)
    c: Vertical(g3)
    c: Coincident(g0,g-1)
    c: DistanceY(g3,g3) = 609.6
    c: DistanceX(g0,g0) = 571.5
FEATURE [PartDesign::FeaturePython] BaseBend  # WARN: FeaturePython — macro-defined, semantics opaque (R4)
  BendSide = 0
  BendSketch = -> Sketch
  length = 100
  radius = 1
  thickness = 1
FEATURE [PartDesign::FeaturePython] Bend  # WARN: FeaturePython — macro-defined, semantics opaque (R4)
  AutoMiter = true
  BaseFeature = -> BaseBend
  BendType = 0
  LengthList = [127]
  ReliefFactor = 0.7
  UseReliefFactor = false
  angle = 90
  baseObject = -> BaseBend [Edge4,Edge10]
  bendAList = [90]
  extend1 = 0
  extend2 = 0
  gap1 = 0
  gap2 = 0
  invert = false
  kfactor = 0.5
  length = 127
  miterangle1 = 0
  miterangle2 = 0
  offset = 0
  radius = 1
  reliefType = 0
  reliefd = 1
  reliefw = 0.8
  sketchflip = false
  sketchinvert = false
  unfold = false
  expr: length = 5"
FEATURE [PartDesign::FeaturePython] Bend001  # WARN: FeaturePython — macro-defined, semantics opaque (R4)
  AutoMiter = true
  BaseFeature = -> Bend
  BendType = 0
  LengthList = [76.2]
  ReliefFactor = 0.7
  UseReliefFactor = false
  angle = 90
  baseObject = -> Bend [Edge43,Edge10]
  bendAList = [90]
  extend1 = 0
  extend2 = 0
  gap1 = 0
  gap2 = 0
  invert = false
  kfactor = 0.5
  length = 76.2
  miterangle1 = 0
  miterangle2 = 0
  offset = 0
  radius = 1
  reliefType = 0
  reliefd = 1
  reliefw = 0.8
  sketchflip = false
  sketchinvert = false
  unfold = false
  expr: length = 3"
FEATURE [PartDesign::FeaturePython] Bend002  # WARN: FeaturePython — macro-defined, semantics opaque (R4)
  AutoMiter = true
  BaseFeature = -> Bend001
  BendType = 0
  LengthList = [457.2]
  ReliefFactor = 0.7
  UseReliefFactor = false
  angle = 90
  baseObject = -> Bend001 [Edge73,Edge9]
  bendAList = [90]
  extend1 = 0
  extend2 = 0
  gap1 = 0
  gap2 = 0
  invert = true
  kfactor = 0.5
  length = 457.2
  miterangle1 = 0
  miterangle2 = 0
  offset = 0
  radius = 1
  reliefType = 0
  reliefd = 1
  reliefw = 0.8
  sketchflip = false
  sketchinvert = false
  unfold = false
  expr: length = 18"
FEATURE [PartDesign::Chamfer] Chamfer
  Angle = 45
  Base = -> Bend002 [Edge100,Edge2,Edge8,Edge108]
  BaseFeature = -> Bend002
  ChamferType = 0
  FlipDirection = false
  Size = 82.55
  Size2 = 1
  SupportTransform = true
  expr: Size = 3.25"
FEATURE [PartDesign::FeaturePython] Bend003  # WARN: FeaturePython — macro-defined, semantics opaque (R4)
  AutoMiter = true
  BaseFeature = -> Chamfer
  BendType = 0
  LengthList = [225.552]
  ReliefFactor = 0.7
  UseReliefFactor = false
  angle = 90
  baseObject = -> Chamfer [Edge11,Edge16,Edge4,Edge18,Edge17,Edge108,Edge117,Edge116,Edge115,Edge114]
  bendAList = [90]
  extend1 = 0
  extend2 = 0
  gap1 = 0
  gap2 = 0
  invert = false
  kfactor = 0.5
  length = 225.552
  miterangle1 = 0
  miterangle2 = 0
  offset = 0
  radius = 1
  reliefType = 0
  reliefd = 1
  reliefw = 0.8
  sketchflip = false
  sketchinvert = false
  unfold = false
  expr: length = 8.880000000000001"
FEATURE [PartDesign::FeaturePython] Bend004  # WARN: FeaturePython — macro-defined, semantics opaque (R4)
  AutoMiter = true
  BaseFeature = -> Bend003
  BendType = 0
  LengthList = [124.46]
  ReliefFactor = 0.7
  UseReliefFactor = false
  angle = 90
  baseObject = -> Bend003 [Edge140,Edge144]
  bendAList = [90]
  extend1 = 0
  extend2 = 0
  gap1 = 0
  gap2 = 0
  invert = false
  kfactor = 0.5
  length = 124.46
  miterangle1 = 0
  miterangle2 = 0
  offset = 0
  radius = 1
  reliefType = 0
  reliefd = 1
  reliefw = 0.8
  sketchflip = false
  sketchinvert = false
  unfold = false
  expr: length = 4.9"
FEATURE [Sketcher::SketchObject] Sketch001
  MapMode = 5
  Placement = pos=(0,0,0) rot=(0.57735,0.57735,0.57735;2.0944rad)
  Support = -> [YZ_Plane001]
  expr: Constraints[16] = 12"
  expr: Constraints[20] = 4"
  expr: Constraints[21] = 23"
  expr: Constraints[22] = 0.5"
  expr: Constraints[23] = 10.5"
  expr: Constraints[24] = 14"
  sketch-geometry (9):
    g0: LineSegment StartX=127 StartY=114.3 StartZ=0 EndX=127 EndY=381 EndZ=0
    g1: LineSegment StartX=127 StartY=381 StartZ=0 EndX=482.6 EndY=381 EndZ=0
    g2: LineSegment StartX=482.6 StartY=381 StartZ=0 EndX=482.6 EndY=114.3 EndZ=0
    g3: LineSegment StartX=482.6 StartY=114.3 StartZ=0 EndX=596.9 EndY=114.3 EndZ=0
    g4: LineSegment StartX=596.9 StartY=114.3 StartZ=0 EndX=596.9 EndY=12.7 EndZ=0
    g5: LineSegment StartX=596.9 StartY=12.7 StartZ=0 EndX=12.7 EndY=12.7 EndZ=0
    g6: LineSegment StartX=12.7 StartY=12.7 StartZ=0 EndX=12.7 EndY=114.3 EndZ=0
    g7: LineSegment StartX=12.7 StartY=114.3 StartZ=0 EndX=127 EndY=114.3 EndZ=0
    g8: LineSegment StartX=304.8 StartY=381 StartZ=0 EndX=304.8 EndY=12.7 EndZ=0
  constraints (25):
    c: Vertical(g0)
    c: Coincident(g0,g1)
    c: Horizontal(g1)
    c: Coincident(g1,g2)
    c: Coincident(g2,g3)
    c: Horizontal(g3)
    c: Coincident(g3,g4)
    c: Vertical(g4)
    c: Coincident(g4,g5)
    c: Coincident(g5,g6)
    c: Vertical(g6)
    c: Coincident(g6,g7)
    c: Horizontal(g7)
    c: Coincident(g0,g7)
    c: PointOnObject(g8,g1)
    c: PointOnObject(g8,g5)
    c: DistanceX(g-1,g8) = 304.8
    c: Symmetric(g1,g0,g8)
    c: Symmetric(g2,g0,g8)
    c: Symmetric(g5,g4,g8)
    c: DistanceY(g4,g4) = 101.6
    c: DistanceX(g5,g5) = 584.2
    c: DistanceY(g-1,g5) = 12.7
    c: DistanceY(g2,g2) = 266.7
    c: DistanceX(g1,g1) = 355.6
FEATURE [Sketcher::SketchObject] Sketch002
  AttachmentOffset = pos=(0,0,571.5) rot=(0,0,1;0rad)
  MapMode = 5
  Placement = pos=(571.5,-1.269e-13,1.269e-13) rot=(0.57735,0.57735,0.57735;2.0944rad)
  Support = -> [YZ_Plane001]
  expr: Constraints[31] = 12"
  expr: .AttachmentOffset.Base.z = 22.5"
  sketch-geometry (11):
    g0: LineSegment StartX=172.3 StartY=465.5 StartZ=0 EndX=437.3 EndY=465.5 EndZ=0
    g1: LineSegment StartX=437.3 StartY=465.5 StartZ=0 EndX=482.3 EndY=420.5 EndZ=0
    g2: LineSegment StartX=482.3 StartY=420.5 StartZ=0 EndX=482.3 EndY=175.5 EndZ=0
    g3: LineSegment StartX=482.3 StartY=175.5 StartZ=0 EndX=437.3 EndY=130.5 EndZ=0
    g4: LineSegment StartX=437.3 StartY=130.5 StartZ=0 EndX=172.3 EndY=130.5 EndZ=0
    g5: LineSegment StartX=172.3 StartY=130.5 StartZ=0 EndX=127.3 EndY=175.5 EndZ=0
    g6: LineSegment StartX=127.3 StartY=175.5 StartZ=0 EndX=127.3 EndY=420.5 EndZ=0
    g7: LineSegment StartX=127.3 StartY=420.5 StartZ=0 EndX=172.3 EndY=465.5 EndZ=0
    g8: LineSegment StartX=304.8 StartY=465.5 StartZ=0 EndX=304.8 EndY=130.5 EndZ=0
    g9: LineSegment StartX=127.3 StartY=298 StartZ=0 EndX=482.3 EndY=298 EndZ=0
    g10: GeomPoint X=304.8 Y=298 Z=0
  constraints (32):
    c: Horizontal(g0)
    c: Coincident(g0,g1)
    c: Coincident(g1,g2)
    c: Vertical(g2)
    c: Coincident(g2,g3)
    c: Coincident(g3,g4)
    c: Horizontal(g4)
    c: Coincident(g4,g5)
    c: Coincident(g5,g6)
    c: Coincident(g6,g7)
    c: Coincident(g7,g0)
    c: Vertical(g6)
    c: Equal(g7,g5)
    c: Equal(g5,g3)
    c: Equal(g3,g1)
    c: Equal(g0,g4)
    c: Equal(g6,g2)
    c: Angle(g7,g0) = 2.35619
    c: Perpendicular(g1,g7)
    c: DistanceX(g6,g1) = 355
    c: DistanceY(g4,g0) = 335
    c: DistanceY(g1,g0) = 45
    c: PointOnObject(g8,g0)
    c: PointOnObject(g8,g4)
    c: PointOnObject(g9,g6)
    c: PointOnObject(g9,g2)
    c: Symmetric(g1,g6,g8)
    c: Symmetric(g3,g0,g9)
    c: PointOnObject(g10,g9)
    c: PointOnObject(g10,g8)
    c: DistanceY(g-1,g10) = 298
    c: DistanceX(g-1,g10) = 304.8
FEATURE [Sketcher::SketchObject] Sketch003
  AttachmentOffset = pos=(0,0,584.2) rot=(0,0,1;0rad)
  MapMode = 5
  Placement = pos=(0,0,584.2) rot=(0,0,1;0rad)
  Support = -> [XY_Plane001]
  expr: Constraints[20] = 12.5"
  expr: Constraints[21] = 14.5"
  expr: Constraints[30] = 12"
  expr: Constraints[31] = 11.25"
  expr: .AttachmentOffset.Base.z = 23"
  sketch-geometry (11):
    g0: LineSegment StartX=127 StartY=443.95 StartZ=0 EndX=172 EndY=488.95 EndZ=0
    g1: LineSegment StartX=172 StartY=488.95 StartZ=0 EndX=399.5 EndY=488.95 EndZ=0
    g2: LineSegment StartX=399.5 StartY=488.95 StartZ=0 EndX=444.5 EndY=443.95 EndZ=0
    g3: LineSegment StartX=444.5 StartY=443.95 StartZ=0 EndX=444.5 EndY=165.65 EndZ=0
    g4: LineSegment StartX=444.5 StartY=165.65 StartZ=0 EndX=399.5 EndY=120.65 EndZ=0
    g5: LineSegment StartX=399.5 StartY=120.65 StartZ=0 EndX=172 EndY=120.65 EndZ=0
    g6: LineSegment StartX=172 StartY=120.65 StartZ=0 EndX=127 EndY=165.65 EndZ=0
    g7: LineSegment StartX=127 StartY=165.65 StartZ=0 EndX=127 EndY=443.95 EndZ=0
    g8: LineSegment StartX=127 StartY=304.8 StartZ=0 EndX=444.5 EndY=304.8 EndZ=0
    g9: LineSegment StartX=285.75 StartY=488.95 StartZ=0 EndX=285.75 EndY=120.65 EndZ=0
    g10: GeomPoint X=285.75 Y=304.8 Z=0
  constraints (32):
    c: Coincident(g0,g1)
    c: Horizontal(g1)
    c: Coincident(g1,g2)
    c: Coincident(g2,g3)
    c: Vertical(g3)
    c: Coincident(g3,g4)
    c: Coincident(g4,g5)
    c: Horizontal(g5)
    c: Coincident(g5,g6)
    c: Coincident(g6,g7)
    c: Coincident(g7,g0)
    c: Vertical(g7)
    c: Equal(g0,g2)
    c: Equal(g2,g4)
    c: Equal(g4,g6)
    c: Angle(g5,g6) = 2.35619
    c: Parallel(g2,g6)
    c: Parallel(g0,g4)
    c: Perpendicular(g0,g6)
    c: DistanceX(g0,g0) = 45
    c: DistanceX(g0,g2) = 317.5
    c: DistanceY(g5,g0) = 368.3
    c: PointOnObject(g8,g7)
    c: PointOnObject(g8,g3)
    c: PointOnObject(g9,g1)
    c: PointOnObject(g9,g5)
    c: PointOnObject(g10,g8)
    c: PointOnObject(g10,g9)
    c: Symmetric(g2,g0,g9)
    c: Symmetric(g1,g4,g8)
    c: DistanceY(g-1,g10) = 304.8
    c: DistanceX(g-1,g10) = 285.75
FEATURE [Sketcher::SketchObject] Sketch004
  MapMode = 5
  Placement = pos=(0,0,0) rot=(1,0,0;1.5708rad)
  Support = -> [XZ_Plane001]
  expr: Constraints[11] = 2.5"
  expr: Constraints[12] = 17.5"
  expr: Constraints[13] = 4.25"
  sketch-geometry (5):
    g0: LineSegment StartX=63.5 StartY=107.95 StartZ=0 EndX=508 EndY=107.95 EndZ=0
    g1: Circle CenterX=63.5 CenterY=107.95 CenterZ=0 NormalX=0 NormalY=0 NormalZ=1 AngleXU=0 Radius=3
    g2: Circle CenterX=88.9 CenterY=107.95 CenterZ=0 NormalX=0 NormalY=0 NormalZ=1 AngleXU=0 Radius=3
    g3: Circle CenterX=508 CenterY=107.95 CenterZ=0 NormalX=0 NormalY=0 NormalZ=1 AngleXU=0 Radius=3
    g4: Circle CenterX=482.6 CenterY=107.95 CenterZ=0 NormalX=0 NormalY=0 NormalZ=1 AngleXU=0 Radius=3
  constraints (14):
    c: Horizontal(g0)
    c: Coincident(g1,g0)
    c: PointOnObject(g2,g0)
    c: Coincident(g3,g0)
    c: PointOnObject(g4,g0)
    c: Equal(g4,g3)
    c: Equal(g3,g2)
    c: Equal(g2,g1)
    c: Diameter(g2) = 6
    c: DistanceX(g1,g2) = 25.4
    c: DistanceX(g4,g3) = 25.4
    c: DistanceX(g-1,g1) = 63.5
    c: DistanceX(g0,g0) = 444.5
    c: DistanceY(g-1,g1) = 107.95
FEATURE [PartDesign::Pocket] Pocket
  BaseFeature = -> Bend004
  Length = 20
  Length2 = 100
  Midplane = true
  Profile = -> Sketch001
  Type = 0
FEATURE [PartDesign::Pocket] Pocket001
  BaseFeature = -> Pocket
  Length = 20
  Length2 = 100
  Midplane = true
  Profile = -> Sketch002
  Type = 0
FEATURE [PartDesign::Pocket] Pocket002
  BaseFeature = -> Pocket001
  Length = 20
  Length2 = 100
  Midplane = true
  Profile = -> Sketch003
  Type = 0
FEATURE [PartDesign::Pocket] Pocket003
  BaseFeature = -> Pocket002
  Length = 5
  Length2 = 100
  Midplane = true
  Profile = -> Sketch004
  Type = 1
FEATURE [Sketcher::SketchObject] Sketch006
  MapMode = 5
  Support = -> [XY_Plane003]
  expr: Constraints[38] = 460
  expr: Constraints[17] = 18"
  expr: Constraints[16] = 22.5"
  expr: Constraints[15] = 3.25"
  sketch-geometry (17):
    g0: LineSegment StartX=0 StartY=0 StartZ=0 EndX=0 EndY=571.5 EndZ=0
    g1: LineSegment StartX=0 StartY=571.5 StartZ=0 EndX=374.65 EndY=571.5 EndZ=0
    g2: LineSegment StartX=374.65 StartY=571.5 StartZ=0 EndX=457.2 EndY=488.95 EndZ=0
    g3: LineSegment StartX=457.2 StartY=488.95 StartZ=0 EndX=457.2 EndY=82.55 EndZ=0
    g4: LineSegment StartX=457.2 StartY=82.55 StartZ=0 EndX=374.65 EndY=0 EndZ=0
    g5: LineSegment StartX=374.65 StartY=0 StartZ=0 EndX=0 EndY=0 EndZ=0
    g6: LineSegment StartX=56.1 StartY=470.75 StartZ=0 EndX=101.1 EndY=515.75 EndZ=0
    g7: LineSegment StartX=101.1 StartY=515.75 StartZ=0 EndX=356.1 EndY=515.75 EndZ=0
    g8: LineSegment StartX=356.1 StartY=515.75 StartZ=0 EndX=401.1 EndY=470.75 EndZ=0
    g9: LineSegment StartX=401.1 StartY=470.75 StartZ=0 EndX=401.1 EndY=100.75 EndZ=0
    g10: LineSegment StartX=401.1 StartY=100.75 StartZ=0 EndX=356.1 EndY=55.75 EndZ=0
    g11: LineSegment StartX=356.1 StartY=55.75 StartZ=0 EndX=101.1 EndY=55.75 EndZ=0
    g12: LineSegment StartX=101.1 StartY=55.75 StartZ=0 EndX=56.1 EndY=100.75 EndZ=0
    g13: LineSegment StartX=56.1 StartY=100.75 StartZ=0 EndX=56.1 EndY=470.75 EndZ=0
    g14: LineSegment StartX=0 StartY=285.75 StartZ=0 EndX=457.2 EndY=285.75 EndZ=0
    g15: LineSegment StartX=228.6 StartY=571.5 StartZ=0 EndX=228.6 EndY=0 EndZ=0
    g16: GeomPoint X=0 Y=488.95 Z=0
  constraints (48):
    c: Coincident(g-1,g0)
    c: Vertical(g0)
    c: Coincident(g0,g1)
    c: Horizontal(g1)
    c: Coincident(g1,g2)
    c: Coincident(g2,g3)
    c: Vertical(g3)
    c: Coincident(g3,g4)
    c: PointOnObject(g4,g-1)
    c: Coincident(g4,g5)
    c: Coincident(g5,g0)
    c: Perpendicular(g2,g4)
    c: Equal(g2,g4)
    c: Angle(g3,g4) = 2.35619
    c: Equal(g2,g4)
    c: DistanceX(g4,g3) = 82.55
    c: DistanceY(g0,g0) = 571.5
    c: DistanceX(g0,g2) = 457.2
    c: Coincident(g6,g7)
    c: Horizontal(g7)
    c: Coincident(g7,g8)
    c: Coincident(g8,g9)
    c: Vertical(g9)
    c: Coincident(g9,g10)
    c: Coincident(g10,g11)
    c: Horizontal(g11)
    c: Coincident(g11,g12)
    c: Coincident(g12,g13)
    c: Coincident(g13,g6)
    c: Vertical(g13)
    c: Angle(g13,g6) = 2.35619
    c: Parallel(g6,g10)
    c: Parallel(g8,g12)
    c: Equal(g6,g12)
    c: Equal(g12,g10)
    c: Equal(g10,g8)
    c: DistanceX(g7,g8) = 45
    c: DistanceX(g6,g8) = 345
    c: DistanceY(g10,g7) = 460
    c: PointOnObject(g14,g0)
    c: PointOnObject(g14,g3)
    c: Symmetric(g0,g0,g14)
    c: Symmetric(g11,g6,g14)
    c: PointOnObject(g15,g1)
    c: PointOnObject(g15,g5)
    c: Symmetric(g6,g8,g15)
    c: PointOnObject(g16,g0)
    c: Symmetric(g16,g2,g15)
FEATURE [PartDesign::FeaturePython] BaseBend001  # WARN: FeaturePython — macro-defined, semantics opaque (R4)
  BendSide = 0
  BendSketch = -> Sketch006
  length = 100
  radius = 1
  thickness = 1
FEATURE [PartDesign::FeaturePython] Bend005  # WARN: FeaturePython — macro-defined, semantics opaque (R4)
  AutoMiter = true
  BaseFeature = -> BaseBend001
  BendType = 0
  LengthList = [101.6]
  ReliefFactor = 0.7
  UseReliefFactor = false
  angle = 90
  baseObject = -> BaseBend001 [Edge18,Edge16,Edge13,Edge10,Edge7]
  bendAList = [90]
  extend1 = 0
  extend2 = 0
  gap1 = 0
  gap2 = 0
  invert = false
  kfactor = 0.5
  length = 101.6
  miterangle1 = 0
  miterangle2 = 0
  offset = 0
  radius = 1
  reliefType = 0
  reliefd = 1
  reliefw = 0.8
  sketchflip = false
  sketchinvert = false
  unfold = false
  expr: length = 4"
FEATURE [PartDesign::FeaturePython] Bend006  # WARN: FeaturePython — macro-defined, semantics opaque (R4)
  AutoMiter = true
  BaseFeature = -> Bend005
  BendType = 0
  LengthList = [12.7]
  ReliefFactor = 0.7
  UseReliefFactor = false
  angle = 90
  baseObject = -> Bend005 [Edge116,Edge113,Edge110,Edge107,Edge10]
  bendAList = [90]
  extend1 = 0
  extend2 = 0
  gap1 = 0
  gap2 = 0
  invert = false
  kfactor = 0.5
  length = 12.7
  miterangle1 = 0
  miterangle2 = 0
  offset = 0
  radius = 1
  reliefType = 0
  reliefd = 1
  reliefw = 0.8
  sketchflip = false
  sketchinvert = false
  unfold = false
  expr: length = 0.5"
FEATURE [PartDesign::FeaturePython] Bend007  # WARN: FeaturePython — macro-defined, semantics opaque (R4)
  AutoMiter = true
  BaseFeature = -> Bend006
  BendType = 0
  LengthList = [50.8]
  ReliefFactor = 0.7
  UseReliefFactor = false
  angle = 90
  baseObject = -> Bend006 [Edge59]
  bendAList = [90]
  extend1 = 0
  extend2 = 0
  gap1 = 0
  gap2 = 0
  invert = false
  kfactor = 0.5
  length = 50.8
  miterangle1 = 0
  miterangle2 = 0
  offset = 0
  radius = 1
  reliefType = 0
  reliefd = 1
  reliefw = 0.8
  sketchflip = false
  sketchinvert = false
  unfold = false
  expr: length = 2"
FEATURE [Sketcher::SketchObject] Sketch007
  ExternalGeometry = -> [Bend007]
  MapMode = 5
  Placement = pos=(-2,0,0) rot=(0.57735,-0.57735,-0.57735;2.0944rad)
  Support = -> [Bend007]
  expr: Constraints[20] = 0.75"
  expr: Constraints[21] = 17.5"
  sketch-geometry (8):
    g0: Circle CenterX=-508 CenterY=21.05 CenterZ=0 NormalX=0 NormalY=0 NormalZ=1 AngleXU=0 Radius=3
    g1: Circle CenterX=-482.6 CenterY=21.05 CenterZ=0 NormalX=0 NormalY=0 NormalZ=1 AngleXU=0 Radius=3
    g2: Circle CenterX=-88.9 CenterY=21.05 CenterZ=0 NormalX=0 NormalY=0 NormalZ=1 AngleXU=0 Radius=3
    g3: Circle CenterX=-63.5 CenterY=21.05 CenterZ=0 NormalX=0 NormalY=0 NormalZ=1 AngleXU=0 Radius=3
    g4: LineSegment StartX=-508 StartY=21.05 StartZ=0 EndX=-285.75 EndY=21.05 EndZ=0
    g5: LineSegment StartX=-285.75 StartY=21.05 StartZ=0 EndX=-63.5 EndY=21.05 EndZ=0
    g6: LineSegment StartX=-571.5 StartY=52.8 StartZ=0 EndX=-285.75 EndY=52.8 EndZ=0
    g7: LineSegment StartX=-285.75 StartY=52.8 StartZ=0 EndX=0 EndY=52.8 EndZ=0
  constraints (22):
    c: DistanceX(g0,g1) = 25.4
    c: DistanceX(g2,g3) = 25.4
    c: Equal(g2,g3)
    c: Equal(g3,g1)
    c: Equal(g1,g0)
    c: Diameter(g1) = 6
    c: Coincident(g4,g0)
    c: Horizontal(g4)
    c: Coincident(g5,g4)
    c: Coincident(g5,g3)
    c: Horizontal(g5)
    c: PointOnObject(g2,g5)
    c: PointOnObject(g1,g4)
    c: Equal(g4,g5)
    c: Coincident(g6,g-3)
    c: Horizontal(g6)
    c: Coincident(g7,g6)
    c: Coincident(g7,g-4)
    c: Equal(g7,g6)
    c: Vertical(g4,g6)
    c: DistanceY(g-3,g0) = 19.05
    c: DistanceX(g0,g3) = 444.5
FEATURE [PartDesign::Pocket] Pocket004
  BaseFeature = -> Bend007
  Length = 5
  Length2 = 100
  Profile = -> Sketch007
  Type = 0
FEATURE [PartDesign::CoordinateSystem] LCS_4
  AttacherType = Attacher::AttachEngine3D
  AttachmentOffset = pos=(0,304.8,0) rot=(0,0,1;0rad)
  MapMode = 1
  Placement = pos=(0,304.8,0) rot=(0,0,1;0rad)
  Support = -> [Pocket003]
  expr: .AttachmentOffset.Base.y = 0.5 * 609.6mm
FEATURE [PartDesign::CoordinateSystem] LCS_5
  AttacherType = Attacher::AttachEngine3D
  MapMode = 45
  Placement = pos=(573.5,304.8,298) rot=(0.707107,0,0.707107;3.14159rad)
  Support = -> [Pocket003]
FEATURE [PartDesign::CoordinateSystem] LCS_6
  AttacherType = Attacher::AttachEngine3D
  MapMode = 45
  Placement = pos=(76.2,611.6,107.95) rot=(0.57735,0.57735,0.57735;4.18879rad)
  Support = -> [Pocket003]
FEATURE [PartDesign::CoordinateSystem] LCS_7
  AttacherType = Attacher::AttachEngine3D
  MapMode = 45
  Placement = pos=(495.3,611.6,107.95) rot=(0.57735,0.57735,0.57735;4.18879rad)
  Support = -> [Pocket003]
FEATURE [PartDesign::Body] Body  label="main_housing"
  Group = -> [Sketch,BaseBend,Bend,Bend001,Bend002,Chamfer,Bend003,Bend004,Sketch001,Sketch002,Sketch003,Sketch004,Pocket,Pocket001,Pocket002,Pocket003,LCS_4,LCS_5,LCS_6,LCS_7]
  Origin = -> Origin001
  Tip = -> Pocket003
FEATURE [PartDesign::CoordinateSystem] LCS_1
  AttacherType = Attacher::AttachEngine3D
  MapMode = 45
  Placement = pos=(228.6,285.75,0) rot=(0,0,1;0rad)
  Support = -> [Pocket004]
FEATURE [PartDesign::CoordinateSystem] LCS_2
  AttacherType = Attacher::AttachEngine3D
  MapMode = 45
  Placement = pos=(-2,76.2,21.05) rot=(0.707107,0,0.707107;3.14159rad)
  Support = -> [Pocket004]
FEATURE [PartDesign::CoordinateSystem] LCS_3
  AttacherType = Attacher::AttachEngine3D
  MapMode = 45
  Placement = pos=(-2,495.3,21.05) rot=(0.707107,0,0.707107;3.14159rad)
  Support = -> [Pocket004]
FEATURE [PartDesign::Body] Body001  label="door"
  Group = -> [Sketch006,BaseBend001,Bend005,Bend006,Bend007,Sketch007,Pocket004,LCS_1,LCS_2,LCS_3]
  Origin = -> Origin003
  Tip = -> Pocket004
---- part enclosure_windows.FCStd = doc fcstd_b9c73843f664 ----
FCSTD DOCUMENT  (FreeCAD 0.19R23578 (Git))
Label: enclosure_windows
License: All rights reserved
LicenseURL: http://en.wikipedia.org/wiki/All_rights_reserved
objects: TechDraw::DrawViewDimExtent×4, PartDesign::CoordinateSystem×4, Sketcher::SketchObject×2, TechDraw::DrawViewPart×2, PartDesign::Pad×2, TechDraw::DrawRichAnno×2, PartDesign::Body×2, TechDraw::DrawSVGTemplate×1, PartDesign::Fillet×1, TechDraw::DrawPage×1
note: 14 computed .brp shape members not serialized (recipe doc carries the construction recipe); baked Part::Feature solids carry a one-line shape summary decoded from their .brp

FEATURE [Sketcher::SketchObject] Sketch001  label="side_piece"
  AttachmentOffset = pos=(400,1,0) rot=(0,0,1;0rad)
  MapMode = 5
  Placement = pos=(400,1,0) rot=(0,0,1;0rad)
  Support = -> [XY_Plane]
  sketch-geometry (52):
    g0: LineSegment StartX=-165 StartY=180 StartZ=0 EndX=-165 EndY=-180 EndZ=0
    g1: LineSegment StartX=-163.536 StartY=-183.536 StartZ=0 EndX=-126.536 EndY=-220.536 EndZ=0
    g2: LineSegment StartX=-123 StartY=-222 StartZ=0 EndX=123 EndY=-222 EndZ=0
    g3: LineSegment StartX=126.536 StartY=-220.536 StartZ=0 EndX=163.536 EndY=-183.536 EndZ=0
    g4: LineSegment StartX=165 StartY=-180 StartZ=0 EndX=165 EndY=180 EndZ=0
    g5: LineSegment StartX=163.536 StartY=183.536 StartZ=0 EndX=126.536 EndY=220.536 EndZ=0
    g6: LineSegment StartX=123 StartY=222 StartZ=0 EndX=-123 EndY=222 EndZ=0
    g7: LineSegment StartX=-126.536 StartY=220.536 StartZ=0 EndX=-163.536 EndY=183.536 EndZ=0
    g8: LineSegment StartX=-108.66 StartY=-165 StartZ=0 EndX=-91.3397 EndY=-135 EndZ=0
    g9: LineSegment StartX=-91.3397 StartY=-135 StartZ=0 EndX=108.66 EndY=-135 EndZ=0
    g10: LineSegment StartX=91.3397 StartY=-165 StartZ=0 EndX=-108.66 EndY=-165 EndZ=0
    g11: ArcOfCircle CenterX=-91.3397 CenterY=-135 CenterZ=0 NormalX=0 NormalY=0 NormalZ=1 AngleXU=0 Radius=2.5 StartAngle=1.5708 EndAngle=4.71239
    g12: ArcOfCircle CenterX=108.66 CenterY=-135 CenterZ=0 NormalX=0 NormalY=0 NormalZ=1 AngleXU=0 Radius=2.5 StartAngle=4.71239 EndAngle=7.85398
    g13: LineSegment StartX=-91.3397 StartY=-137.5 StartZ=0 EndX=108.66 EndY=-137.5 EndZ=0
    g14: LineSegment StartX=-91.3397 StartY=-132.5 StartZ=0 EndX=108.66 EndY=-132.5 EndZ=0
    g15: ArcOfCircle CenterX=-100 CenterY=-150 CenterZ=0 NormalX=0 NormalY=0 NormalZ=1 AngleXU=0 Radius=2.5 StartAngle=1.5708 EndAngle=4.71239
    g16: ArcOfCircle CenterX=100 CenterY=-150 CenterZ=0 NormalX=0 NormalY=0 NormalZ=1 AngleXU=0 Radius=2.5 StartAngle=4.71239 EndAngle=7.85398
    g17: LineSegment StartX=-100 StartY=-152.5 StartZ=0 EndX=100 EndY=-152.5 EndZ=0
    g18: LineSegment StartX=-100 StartY=-147.5 StartZ=0 EndX=100 EndY=-147.5 EndZ=0
    g19: ArcOfCircle CenterX=-108.66 CenterY=-165 CenterZ=0 NormalX=0 NormalY=0 NormalZ=1 AngleXU=0 Radius=2.5 StartAngle=1.5708 EndAngle=4.71239
    g20: ArcOfCircle CenterX=91.3397 CenterY=-165 CenterZ=0 NormalX=0 NormalY=0 NormalZ=1 AngleXU=0 Radius=2.5 StartAngle=4.71239 EndAngle=7.85398
    g21: LineSegment StartX=-108.66 StartY=-167.5 StartZ=0 EndX=91.3397 EndY=-167.5 EndZ=0
    g22: LineSegment StartX=-108.66 StartY=-162.5 StartZ=0 EndX=91.3397 EndY=-162.5 EndZ=0
    g23: LineSegment StartX=44.2199 StartY=160.5 StartZ=0 EndX=85.7801 EndY=160.5 EndZ=0
    g24: LineSegment StartX=103.5 StartY=101.22 StartZ=0 EndX=103.5 EndY=142.78 EndZ=0
    g25: LineSegment StartX=85.7801 StartY=83.5 StartZ=0 EndX=44.2199 EndY=83.5 EndZ=0
    g26: LineSegment StartX=26.5 StartY=101.22 StartZ=0 EndX=26.5 EndY=142.78 EndZ=0
    g27: ArcOfCircle CenterX=65 CenterY=122 CenterZ=0 NormalX=0 NormalY=0 NormalZ=1 AngleXU=0 Radius=43.75 StartAngle=5.20732 EndAngle=5.78825
    g28: ArcOfCircle CenterX=65 CenterY=122 CenterZ=0 NormalX=0 NormalY=0 NormalZ=1 AngleXU=0 Radius=43.75 StartAngle=0.494934 EndAngle=1.07586
    g29: ArcOfCircle CenterX=65 CenterY=122 CenterZ=0 NormalX=0 NormalY=0 NormalZ=1 AngleXU=0 Radius=43.75 StartAngle=2.06573 EndAngle=2.64666
    g30: ArcOfCircle CenterX=65 CenterY=122 CenterZ=0 NormalX=0 NormalY=0 NormalZ=1 AngleXU=0 Radius=43.75 StartAngle=3.63653 EndAngle=4.21745
    g31: LineSegment StartX=29.25 StartY=157.75 StartZ=0 EndX=100.75 EndY=157.75 EndZ=0
    g32: LineSegment StartX=100.75 StartY=157.75 StartZ=0 EndX=100.75 EndY=86.25 EndZ=0
    g33: LineSegment StartX=100.75 StartY=86.25 StartZ=0 EndX=29.25 EndY=86.25 EndZ=0
    g34: LineSegment StartX=29.25 StartY=86.25 StartZ=0 EndX=29.25 EndY=157.75 EndZ=0
    g35: LineSegment StartX=29.25 StartY=157.75 StartZ=0 EndX=100.75 EndY=86.25 EndZ=0
    g36: LineSegment StartX=100.75 StartY=157.75 StartZ=0 EndX=29.25 EndY=86.25 EndZ=0
    g37: Circle CenterX=29.25 CenterY=157.75 CenterZ=0 NormalX=0 NormalY=0 NormalZ=1 AngleXU=0 Radius=2.5
    g38: Circle CenterX=100.75 CenterY=157.75 CenterZ=0 NormalX=0 NormalY=0 NormalZ=1 AngleXU=0 Radius=2.5
    g39: Circle CenterX=100.75 CenterY=86.25 CenterZ=0 NormalX=0 NormalY=0 NormalZ=1 AngleXU=0 Radius=2.5
    g40: Circle CenterX=29.25 CenterY=86.25 CenterZ=0 NormalX=0 NormalY=0 NormalZ=1 AngleXU=0 Radius=2.5
    g41: LineSegment StartX=108.66 StartY=-135 StartZ=0 EndX=100 EndY=-150 EndZ=0
    g42: LineSegment StartX=100 StartY=-150 StartZ=0 EndX=91.3397 EndY=-165 EndZ=0
    g43: ArcOfCircle CenterX=-123 CenterY=217 CenterZ=0 NormalX=0 NormalY=0 NormalZ=1 AngleXU=0 Radius=5 StartAngle=1.5708 EndAngle=2.35619
    g44: ArcOfCircle CenterX=-160 CenterY=180 CenterZ=0 NormalX=0 NormalY=0 NormalZ=1 AngleXU=0 Radius=5 StartAngle=2.35619 EndAngle=3.14159
    g45: ArcOfCircle CenterX=123 CenterY=217 CenterZ=0 NormalX=0 NormalY=0 NormalZ=1 AngleXU=0 Radius=5 StartAngle=0.785398 EndAngle=1.5708
    g46: ArcOfCircle CenterX=160 CenterY=180 CenterZ=0 NormalX=0 NormalY=0 NormalZ=1 AngleXU=0 Radius=5 StartAngle=5e-16 EndAngle=0.785398
    g47: ArcOfCircle CenterX=160 CenterY=-180 CenterZ=0 NormalX=0 NormalY=0 NormalZ=1 AngleXU=0 Radius=5 StartAngle=5.49779 EndAngle=6.28319
    g48: ArcOfCircle CenterX=123 CenterY=-217 CenterZ=0 NormalX=0 NormalY=0 NormalZ=1 AngleXU=0 Radius=5 StartAngle=4.71239 EndAngle=5.49779
    g49: ArcOfCircle CenterX=-160 CenterY=-180 CenterZ=0 NormalX=0 NormalY=0 NormalZ=1 AngleXU=0 Radius=5 StartAngle=3.14159 EndAngle=3.92699
    g50: ArcOfCircle CenterX=-123 CenterY=-217 CenterZ=0 NormalX=0 NormalY=0 NormalZ=1 AngleXU=0 Radius=5 StartAngle=3.92699 EndAngle=4.71239
    g51: GeomPoint X=308.66 Y=-135 Z=0
  constraints (131):
    c: Horizontal(g2)
    c: Vertical(g4)
    c: Horizontal(g6)
    c: Coincident(g8,g9)
    c: Horizontal(g9)
    c: Coincident(g10,g8)
    c: Horizontal(g10)
    c: Tangent(g11,g14)
    c: Tangent(g11,g13)
    c: Tangent(g13,g12)
    c: Tangent(g14,g12)
    c: Horizontal(g13)
    c: Coincident(g11,g8)
    c: Tangent(g15,g18)
    c: Tangent(g15,g17)
    c: Tangent(g17,g16)
    c: Tangent(g18,g16)
    c: Horizontal(g17)
    c: PointOnObject(g15,g8)
    c: Tangent(g19,g22)
    c: Tangent(g19,g21)
    c: Tangent(g21,g20)
    c: Tangent(g22,g20)
    c: Horizontal(g21)
    c: Coincident(g19,g8)
    c: Horizontal(g23)
    c: Horizontal(g25)
    c: Vertical(g24)
    c: Vertical(g26)
    c: PointOnObject(g23,g27)
    c: PointOnObject(g26,g27)
    c: PointOnObject(g23,g27)
    c: PointOnObject(g26,g27)
    c: Coincident(g27,g25)
    c: Coincident(g30,g25)
    c: Equal(g27,g28)
    c: Coincident(g27,g24)
    c: Coincident(g28,g24)
    c: Coincident(g27,g28)
    c: Equal(g28,g29)
    c: PointOnObject(g28,g23)
    c: PointOnObject(g29,g23)
    c: Coincident(g28,g29)
    c: Equal(g29,g30)
    c: PointOnObject(g29,g26)
    c: PointOnObject(g30,g26)
    c: Coincident(g29,g30)
    c: Equal(g26,g23)
    c: Equal(g23,g24)
    c: Equal(g24,g25)
    c: Diameter(g29) = 87.5
    c: DistanceY(g25,g23) = 77
    c: Coincident(g31,g32)
    c: Coincident(g32,g33)
    c: Coincident(g33,g34)
    c: Coincident(g34,g31)
    c: Horizontal(g31)
    c: Horizontal(g33)
    c: Vertical(g32)
    c: Vertical(g34)
    c: Coincident(g35,g31)
    c: Coincident(g35,g32)
    c: Coincident(g36,g31)
    c: Coincident(g36,g33)
    c: PointOnObject(g27,g36)
    c: PointOnObject(g27,g35)
    c: Equal(g31,g34)
    c: DistanceY(g34,g34) = 71.5
    c: Coincident(g37,g31)
    c: Coincident(g38,g31)
    c: Coincident(g39,g32)
    c: Coincident(g40,g33)
    c: Equal(g40,g37)
    c: Equal(g37,g38)
    c: Equal(g38,g39)
    c: Diameter(g38) = 5
    c: Vertical(g0)
    c: Coincident(g12,g9)
    c: Equal(g20,g16)
    c: Equal(g16,g12)
    c: DistanceY(g12,g12) = 5
    c: Coincident(g41,g12)
    c: Coincident(g41,g16)
    c: Coincident(g42,g16)
    c: Coincident(g42,g20)
    c: Equal(g41,g42)
    c: Parallel(g41,g42)
    c: DistanceY(g19,g11) = 30
    c: Angle(g10,g8) = 1.0472
    c: Angle(g42,g10) = 2.0944
    c: Coincident(g10,g20)
    c: Tangent(g6,g43) = -1.5708
    c: Tangent(g7,g43) = -1.5708
    c: Tangent(g0,g44) = -1.5708
    c: Tangent(g7,g44) = -1.5708
    c: Tangent(g5,g45) = -1.5708
    c: Tangent(g6,g45) = -1.5708
    c: Tangent(g4,g46) = -1.5708
    c: Tangent(g5,g46) = -1.5708
    c: Tangent(g3,g47) = -1.5708
    c: Tangent(g4,g47) = -1.5708
    c: Tangent(g2,g48) = -1.5708
    c: Tangent(g3,g48) = -1.5708
    c: Tangent(g0,g49) = -1.5708
    c: Tangent(g1,g49) = -1.5708
    c: Tangent(g1,g50) = -1.5708
    c: Tangent(g2,g50) = -1.5708
    c: Equal(g44,g43)
    c: Equal(g43,g45)
    c: Equal(g45,g46)
    c: Equal(g46,g47)
    c: Equal(g47,g48)
    c: Equal(g48,g50)
    c: Equal(g50,g49)
    c: Radius(g49) = 5
    c: Parallel(g7,g3)
    c: Parallel(g5,g1)
    c: Perpendicular(g5,g7)
    c: DistanceX(g0,g4) = 330
    c: Symmetric(g0,g4,g-2)
    c: Symmetric(g6,g2,g-1)
    c: DistanceY(g2,g6) = 444
    c: Angle(g6,g5) = 2.35619
    c: Equal(g3,g1)
    c: DistanceX(g0,g2) = 42
    c: DistanceX(g9,g9) = 200
    c: Symmetric(g11,g51,g12)
    c: Symmetric(g15,g16,g-2)
    c: DistanceY(g16,g-1) = 150
    c: DistanceY(g27,g6) = 100
    c: DistanceX(g27,g4) = 100
FEATURE [TechDraw::DrawSVGTemplate] Template
  EditableTexts = Author=AN; DWG_num=x; Date=06/08/2020; Revision=1; Scale=1:4; Subtitle=Material: 3/16" Arrylic sheet; Title=Enclosure window panels
  Height = 215.9
  Orientation = 1
  Width = 279.4
FEATURE [TechDraw::DrawViewPart] View
  CoarseView = false
  Direction = (0,0,1)
  Focus = 100
  HardHidden = false
  IsoCount = 0
  IsoHidden = false
  IsoVisible = false
  LockPosition = false
  Perspective = false
  Rotation = 0
  Scale = 0.25
  ScaleType = 0
  SeamHidden = false
  SeamVisible = true
  SmoothHidden = false
  SmoothVisible = true
  Source = -> [Sketch001]
  X = 209.743
  XDirection = (1,0,0)
  Y = 125.367
FEATURE [PartDesign::Pad] Pad
  Direction = (1,1,1)
  Length = 4.7625
  Length2 = 100
  Midplane = true
  Profile = -> Sketch001
  Type = 0
  expr: Length = 3in / 16
FEATURE [Sketcher::SketchObject] Sketch002  label="top_piece001"
  MapMode = 5
  Support = -> [XY_Plane001]
  sketch-geometry (41):
    g0: LineSegment StartX=-170.5 StartY=117.5 StartZ=0 EndX=-170.5 EndY=-117.5 EndZ=0
    g1: LineSegment StartX=-169.036 StartY=-121.036 StartZ=0 EndX=-132.036 EndY=-158.036 EndZ=0
    g2: LineSegment StartX=-128.5 StartY=-159.5 StartZ=0 EndX=128.5 EndY=-159.5 EndZ=0
    g3: LineSegment StartX=132.036 StartY=-158.036 StartZ=0 EndX=169.036 EndY=-121.036 EndZ=0
    g4: LineSegment StartX=170.5 StartY=-117.5 StartZ=0 EndX=170.5 EndY=117.5 EndZ=0
    g5: LineSegment StartX=169.036 StartY=121.036 StartZ=0 EndX=132.036 EndY=158.036 EndZ=0
    g6: LineSegment StartX=128.5 StartY=159.5 StartZ=0 EndX=-128.5 EndY=159.5 EndZ=0
    g7: LineSegment StartX=-132.036 StartY=158.036 StartZ=0 EndX=-169.036 EndY=121.036 EndZ=0
    g8: Circle CenterX=0 CenterY=0 CenterZ=0 NormalX=0 NormalY=0 NormalZ=1 AngleXU=0 Radius=55
    g9: ArcOfCircle CenterX=128.5 CenterY=154.5 CenterZ=0 NormalX=0 NormalY=0 NormalZ=1 AngleXU=0 Radius=5 StartAngle=0.785398 EndAngle=1.5708
    g10: ArcOfCircle CenterX=165.5 CenterY=117.5 CenterZ=0 NormalX=0 NormalY=0 NormalZ=1 AngleXU=0 Radius=5 StartAngle=1.4e-15 EndAngle=0.785398
    g11: ArcOfCircle CenterX=165.5 CenterY=-117.5 CenterZ=0 NormalX=0 NormalY=0 NormalZ=1 AngleXU=0 Radius=5 StartAngle=5.49779 EndAngle=6.28319
    g12: ArcOfCircle CenterX=128.5 CenterY=-154.5 CenterZ=0 NormalX=0 NormalY=0 NormalZ=1 AngleXU=0 Radius=5 StartAngle=4.71239 EndAngle=5.49779
    g13: ArcOfCircle CenterX=-128.5 CenterY=-154.5 CenterZ=0 NormalX=0 NormalY=0 NormalZ=1 AngleXU=0 Radius=5 StartAngle=3.92699 EndAngle=4.71239
    g14: ArcOfCircle CenterX=-165.5 CenterY=-117.5 CenterZ=0 NormalX=0 NormalY=0 NormalZ=1 AngleXU=0 Radius=5 StartAngle=3.14159 EndAngle=3.92699
    g15: ArcOfCircle CenterX=-128.5 CenterY=154.5 CenterZ=0 NormalX=0 NormalY=0 NormalZ=1 AngleXU=0 Radius=5 StartAngle=1.5708 EndAngle=2.35619
    g16: ArcOfCircle CenterX=-165.5 CenterY=117.5 CenterZ=0 NormalX=0 NormalY=0 NormalZ=1 AngleXU=0 Radius=5 StartAngle=2.35619 EndAngle=3.14159
    g17: LineSegment StartX=-94.8683 StartY=5 StartZ=0 EndX=-64.8074 EndY=5 EndZ=0
    g18: LineSegment StartX=94.8683 StartY=-5 StartZ=0 EndX=64.8074 EndY=-5 EndZ=0
    g19: LineSegment StartX=-5 StartY=94.8683 StartZ=0 EndX=-5 EndY=64.8074 EndZ=0
    g20: LineSegment StartX=5 StartY=94.8683 StartZ=0 EndX=5 EndY=64.8074 EndZ=0
    g21: ArcOfCircle CenterX=0 CenterY=0 CenterZ=0 NormalX=0 NormalY=0 NormalZ=1 AngleXU=0 Radius=65 StartAngle=1.6478 EndAngle=3.06459
    g22: ArcOfCircle CenterX=0 CenterY=0 CenterZ=0 NormalX=0 NormalY=0 NormalZ=1 AngleXU=0 Radius=95 StartAngle=1.62345 EndAngle=3.08894
    g23: LineSegment StartX=64.8074 StartY=5 StartZ=0 EndX=94.8683 EndY=5 EndZ=0
    g24: LineSegment StartX=-5 StartY=-64.8074 StartZ=0 EndX=-5 EndY=-94.8683 EndZ=0
    g25: LineSegment StartX=-64.8074 StartY=-5 StartZ=0 EndX=-94.8683 EndY=-5 EndZ=0
    g26: LineSegment StartX=5 StartY=-64.8074 StartZ=0 EndX=5 EndY=-94.8683 EndZ=0
    g27: ArcOfCircle CenterX=0 CenterY=0 CenterZ=0 NormalX=0 NormalY=0 NormalZ=1 AngleXU=0 Radius=95 StartAngle=0.0526559 EndAngle=1.51814
    g28: ArcOfCircle CenterX=0 CenterY=0 CenterZ=0 NormalX=0 NormalY=0 NormalZ=1 AngleXU=0 Radius=65 StartAngle=0.0769991 EndAngle=1.4938
    g29: ArcOfCircle CenterX=0 CenterY=0 CenterZ=0 NormalX=0 NormalY=0 NormalZ=1 AngleXU=0 Radius=65 StartAngle=3.21859 EndAngle=4.63539
    g30: ArcOfCircle CenterX=0 CenterY=0 CenterZ=0 NormalX=0 NormalY=0 NormalZ=1 AngleXU=0 Radius=95 StartAngle=3.19425 EndAngle=4.65973
    g31: ArcOfCircle CenterX=0 CenterY=0 CenterZ=0 NormalX=0 NormalY=0 NormalZ=1 AngleXU=0 Radius=65 StartAngle=4.78939 EndAngle=6.20619
    g32: ArcOfCircle CenterX=0 CenterY=0 CenterZ=0 NormalX=0 NormalY=0 NormalZ=1 AngleXU=0 Radius=95 StartAngle=4.76504 EndAngle=6.23053
    g33: Circle CenterX=-77 CenterY=77 CenterZ=0 NormalX=0 NormalY=0 NormalZ=1 AngleXU=0 Radius=2.5
    g34: Circle CenterX=77 CenterY=-77 CenterZ=0 NormalX=0 NormalY=0 NormalZ=1 AngleXU=0 Radius=2.5
    g35: Circle CenterX=-77 CenterY=-77 CenterZ=0 NormalX=0 NormalY=0 NormalZ=1 AngleXU=0 Radius=2.5
    g36: Circle CenterX=77 CenterY=77 CenterZ=0 NormalX=0 NormalY=0 NormalZ=1 AngleXU=0 Radius=2.5
    g37: LineSegment StartX=-77 StartY=77 StartZ=0 EndX=77 EndY=77 EndZ=0
    g38: LineSegment StartX=77 StartY=77 StartZ=0 EndX=77 EndY=-77 EndZ=0
    g39: LineSegment StartX=77 StartY=-77 StartZ=0 EndX=-77 EndY=-77 EndZ=0
    g40: LineSegment StartX=-77 StartY=-77 StartZ=0 EndX=-77 EndY=77 EndZ=0
  constraints (100):
    c: Vertical(g0)
    c: Horizontal(g2)
    c: Vertical(g4)
    c: Horizontal(g6)
    c: Coincident(g8,g-1)
    c: Tangent(g5,g9) = -1.5708
    c: Tangent(g6,g9) = -1.5708
    c: Tangent(g4,g10) = -1.5708
    c: Tangent(g5,g10) = -1.5708
    c: Tangent(g3,g11) = -1.5708
    c: Tangent(g4,g11) = -1.5708
    c: Tangent(g2,g12) = -1.5708
    c: Tangent(g3,g12) = -1.5708
    c: Tangent(g1,g13) = -1.5708
    c: Tangent(g2,g13) = -1.5708
    c: Tangent(g0,g14) = -1.5708
    c: Tangent(g1,g14) = -1.5708
    c: Tangent(g6,g15) = -1.5708
    c: Tangent(g7,g15) = -1.5708
    c: Tangent(g0,g16) = -1.5708
    c: Tangent(g7,g16) = -1.5708
    c: Parallel(g5,g1)
    c: Parallel(g7,g3)
    c: Perpendicular(g5,g7)
    c: Angle(g7,g6) = 2.35619
    c: Equal(g7,g5)
    c: Equal(g5,g3)
    c: Equal(g3,g1)
    c: Symmetric(g0,g4,g-2)
    c: Symmetric(g6,g2,g-1)
    c: Equal(g14,g13)
    c: Equal(g13,g12)
    c: Equal(g12,g11)
    c: Equal(g11,g10)
    c: Equal(g10,g9)
    c: Radius(g10) = 5
    c: DistanceX(g0,g6) = 42
    c: DistanceX(g0,g4) = 341
    c: DistanceY(g2,g6) = 319
    c: Horizontal(g17)
    c: Horizontal(g18)
    c: Vertical(g19)
    c: Vertical(g20)
    c: Diameter(g8) = 110
    c: Coincident(g21,g8)
    c: Coincident(g22,g8)
    c: Tangent(g17,g23)
    c: Tangent(g19,g24)
    c: Tangent(g18,g25)
    c: Tangent(g20,g26)
    c: Coincident(g21,g19)
    c: Coincident(g28,g20)
    c: Coincident(g22,g27)
    c: Equal(g21,g28)
    c: Coincident(g21,g28)
    c: Coincident(g23,g28)
    c: Coincident(g18,g31)
    c: Coincident(g18,g32)
    c: Coincident(g23,g27)
    c: Coincident(g19,g22)
    c: Coincident(g20,g27)
    c: Equal(g21,g29)
    c: Coincident(g21,g17)
    c: Coincident(g21,g29)
    c: Equal(g22,g30)
    c: Coincident(g22,g30)
    c: Coincident(g17,g22)
    c: Coincident(g25,g30)
    c: Coincident(g25,g29)
    c: Equal(g29,g31)
    c: Coincident(g29,g24)
    c: Coincident(g31,g26)
    c: Coincident(g29,g31)
    c: Coincident(g30,g32)
    c: Coincident(g26,g32)
    c: Coincident(g24,g30)
    c: Symmetric(g20,g19,g-2)
    c: Diameter(g28) = 130
    c: Diameter(g27) = 190
    c: Symmetric(g18,g23,g-1)
    c: DistanceY(g18,g23) = 10
    c: DistanceX(g19,g20) = 10
    c: Coincident(g37,g38)
    c: Coincident(g38,g39)
    c: Coincident(g39,g40)
    c: Coincident(g40,g37)
    c: Horizontal(g39)
    c: Vertical(g38)
    c: Coincident(g37,g33)
    c: Coincident(g38,g34)
    c: Coincident(g36,g37)
    c: Coincident(g35,g39)
    c: Equal(g40,g39)
    c: Symmetric(g35,g33,g-1)
    c: Symmetric(g33,g36,g-2)
    c: Equal(g36,g33)
    c: Equal(g33,g35)
    c: Equal(g35,g34)
    c: Diameter(g34) = 5
    c: DistanceX(g37,g37) = 154
FEATURE [PartDesign::Pad] Pad001
  Direction = (1,1,1)
  Length = 4.7625
  Length2 = 100
  Midplane = true
  Profile = -> Sketch002
  Type = 0
  expr: Length = 3in / 16
FEATURE [PartDesign::Fillet] Fillet
  Base = -> Pad001 [Edge80,Edge88,Edge89,Edge77,Edge76,Edge59,Edge83,Edge53,Edge52,Edge68,Edge65,Edge56,Edge95,Edge71,Edge64,Edge92]
  BaseFeature = -> Pad001
  Radius = 5
  SupportTransform = true
FEATURE [TechDraw::DrawViewPart] View001
  CoarseView = false
  Direction = (0,0,1)
  Focus = 100
  HardHidden = false
  IsoCount = 0
  IsoHidden = false
  IsoVisible = false
  LockPosition = false
  Perspective = false
  Rotation = 0
  Scale = 0.25
  ScaleType = 0
  SeamHidden = false
  SeamVisible = true
  SmoothHidden = false
  SmoothVisible = true
  Source = -> [Fillet]
  X = 86.9163
  XDirection = (1,0,0)
  Y = 123.25
FEATURE [TechDraw::DrawViewDimExtent] DimExtent
  Arbitrary = false
  ArbitraryTolerances = false
  CosmeticTags = 288ce400-6803-4ff3-8631-b07757546f7d | fa33bd96-712d-4188-b98a-81c6ac7bc85e
  DirExtent = 0
  FormatSpec = %.0f
  FormatSpecOverTolerance = %+.2f
  FormatSpecUnderTolerance = %+.2f
  Inverted = false
  LockPosition = false
  MeasureType = 1
  OverTolerance = 0
  References2D = -> [View001]
  Rotation = 0
  ScaleType = 0
  Source = -> [View001]
  TheoreticalExact = false
  Type = 1
  UnderTolerance = 0
  X = -6.69232
  Y = 53.5385
FEATURE [TechDraw::DrawViewDimExtent] DimExtent001
  Arbitrary = false
  ArbitraryTolerances = false
  CosmeticTags = 8f42bda8-79a3-4fe8-b8ad-edf73163d0b5 | 82f00fcd-74c2-4853-aa97-94300f8e63c0
  DirExtent = 1
  FormatSpec = %.0f
  FormatSpecOverTolerance = %+.2f
  FormatSpecUnderTolerance = %+.2f
  Inverted = false
  LockPosition = false
  MeasureType = 1
  OverTolerance = 0
  References2D = -> [View001]
  Rotation = 0
  ScaleType = 0
  Source = -> [View001]
  TheoreticalExact = false
  Type = 2
  UnderTolerance = 0
  X = -61.6857
  Y = -4.9465
FEATURE [TechDraw::DrawViewDimExtent] DimExtent003
  Arbitrary = false
  ArbitraryTolerances = false
  CosmeticTags = 2a4c7c9a-20be-468c-a347-82470489cc8d | 03f315e3-f9e5-4f8a-bf5f-073e1e309c87
  DirExtent = 1
  FormatSpec = %.0f
  FormatSpecOverTolerance = %+.2f
  FormatSpecUnderTolerance = %+.2f
  Inverted = false
  LockPosition = false
  MeasureType = 1
  OverTolerance = 0
  References2D = -> [View]
  Rotation = 0
  ScaleType = 0
  Source = -> [View]
  TheoreticalExact = false
  Type = 2
  UnderTolerance = 0
  X = -56.7392
  Y = 5.81941
FEATURE [TechDraw::DrawViewDimExtent] DimExtent004
  Arbitrary = false
  ArbitraryTolerances = false
  CosmeticTags = a94bd8f1-ed9f-4015-9f45-3e27d023ae27 | ae9efa26-c7d3-4067-8a4b-398840287b2f
  DirExtent = 0
  FormatSpec = %.0f
  FormatSpecOverTolerance = %+.2f
  FormatSpecUnderTolerance = %+.2f
  Inverted = false
  LockPosition = false
  MeasureType = 1
  OverTolerance = 0
  References2D = -> [View]
  Rotation = 0
  ScaleType = 0
  Source = -> [View]
  TheoreticalExact = false
  Type = 1
  UnderTolerance = 0
  X = -7.8562
  Y = 65.7593
FEATURE [TechDraw::DrawRichAnno] RichTextAnnotation
  AnnoParent = -> View001
  AnnoText = <!DOCTYPE HTML PUBLIC "-//W3C//DTD HTML 4.0//EN" "http://www.w3.org/TR/REC-html40/strict.dtd">\n<html><head><meta name="qrichtext" content="1" /><style type="text/css">\np, li { white-space: pre-wrap; }\n</style></head><body style=" font-family:'Cantarell'; font-size:10pt; font-weight:400; font-style:normal;">\n<p style=" margin-top:0px; margin-bottom:0px; margin-left:0px; margin-right:0px; -qt-block-indent:0; text-indent:0px;"><span style=" font-family:'Bitstream Vera Sans'; font-size:8pt; text-decoration: underline; color:#000000;">Top panel - 1 Required</span></p>\n<p style=" margin-top:0px; margin-bottom:0px; margin-left:0px; margin-right:0px; -qt-block-indent:0; text-indent:0px;"><span style=" font-family:'Bitstream Vera Sans'; font-size:8pt; color:#000000;">     top_panel.dxf</span></p></body></html>
  LockPosition = false
  MaxWidth = -1
  Rotation = 0
  ScaleType = 0
  ShowFrame = false
  X = -1.16388
  Y = -56.1573
FEATURE [TechDraw::DrawRichAnno] RichTextAnnotation001
  AnnoParent = -> View
  AnnoText = <!DOCTYPE HTML PUBLIC "-//W3C//DTD HTML 4.0//EN" "http://www.w3.org/TR/REC-html40/strict.dtd">\n<html><head><meta name="qrichtext" content="1" /><style type="text/css">\np, li { white-space: pre-wrap; }\n</style></head><body style=" font-family:'Cantarell'; font-size:10pt; font-weight:400; font-style:normal;">\n<p style=" margin-top:0px; margin-bottom:0px; margin-left:0px; margin-right:0px; -qt-block-indent:0; text-indent:0px;"><span style=" font-family:'Bitstream Vera Sans'; font-size:8pt; text-decoration: underline; color:#000000;">Side panel - 2 Required</span></p>\n<p style=" margin-top:0px; margin-bottom:0px; margin-left:0px; margin-right:0px; -qt-block-indent:0; text-indent:0px;"><span style=" font-family:'Bitstream Vera Sans'; font-size:8pt; color:#000000;">    side_panel.dxf</span></p></body></html>
  LockPosition = false
  MaxWidth = -1
  Rotation = 0
  ScaleType = 0
  ShowFrame = false
  X = 2.32776
  Y = -66.3412
FEATURE [TechDraw::DrawPage] Page
  KeepUpdated = false
  NextBalloonIndex = 1
  ProjectionType = 0
  Template = -> Template
  Views = -> [View,View001,DimExtent,DimExtent001,DimExtent003,DimExtent004,RichTextAnnotation,RichTextAnnotation001]
FEATURE [PartDesign::CoordinateSystem] LCS_1
  AttacherType = Attacher::AttachEngine3D
  MapMode = 45
  Placement = pos=(2.625e-13,4.1e-15,0) rot=(0,0,1;0rad)
  Support = -> [Fillet]
FEATURE [PartDesign::Body] Body001  label="top_acrylic_panel"
  Group = -> [Sketch002,Pad001,Fillet,LCS_1]
  Origin = -> Origin001
  Tip = -> Fillet
FEATURE [PartDesign::CoordinateSystem] LCS_2
  AttacherType = Attacher::AttachEngine3D
  MapMode = 45
  Placement = pos=(400,1,0) rot=(0,0,1;0rad)
  Support = -> [Pad]
FEATURE [PartDesign::CoordinateSystem] LCS_3
  AttacherType = Attacher::AttachEngine3D
  MapMode = 45
  Placement = pos=(465,123,2.38125) rot=(0,0,1;0rad)
  Support = -> [Pad]
FEATURE [PartDesign::CoordinateSystem] LCS_4
  AttacherType = Attacher::AttachEngine3D
  MapMode = 45
  Placement = pos=(465,123,-2.38125) rot=(0,0,1;0rad)
  Support = -> [Pad]
FEATURE [PartDesign::Body] Body  label="side_acrylic_panel"
  Group = -> [Sketch001,Pad,LCS_2,LCS_3,LCS_4]
  Origin = -> Origin
  Tip = -> Pad
